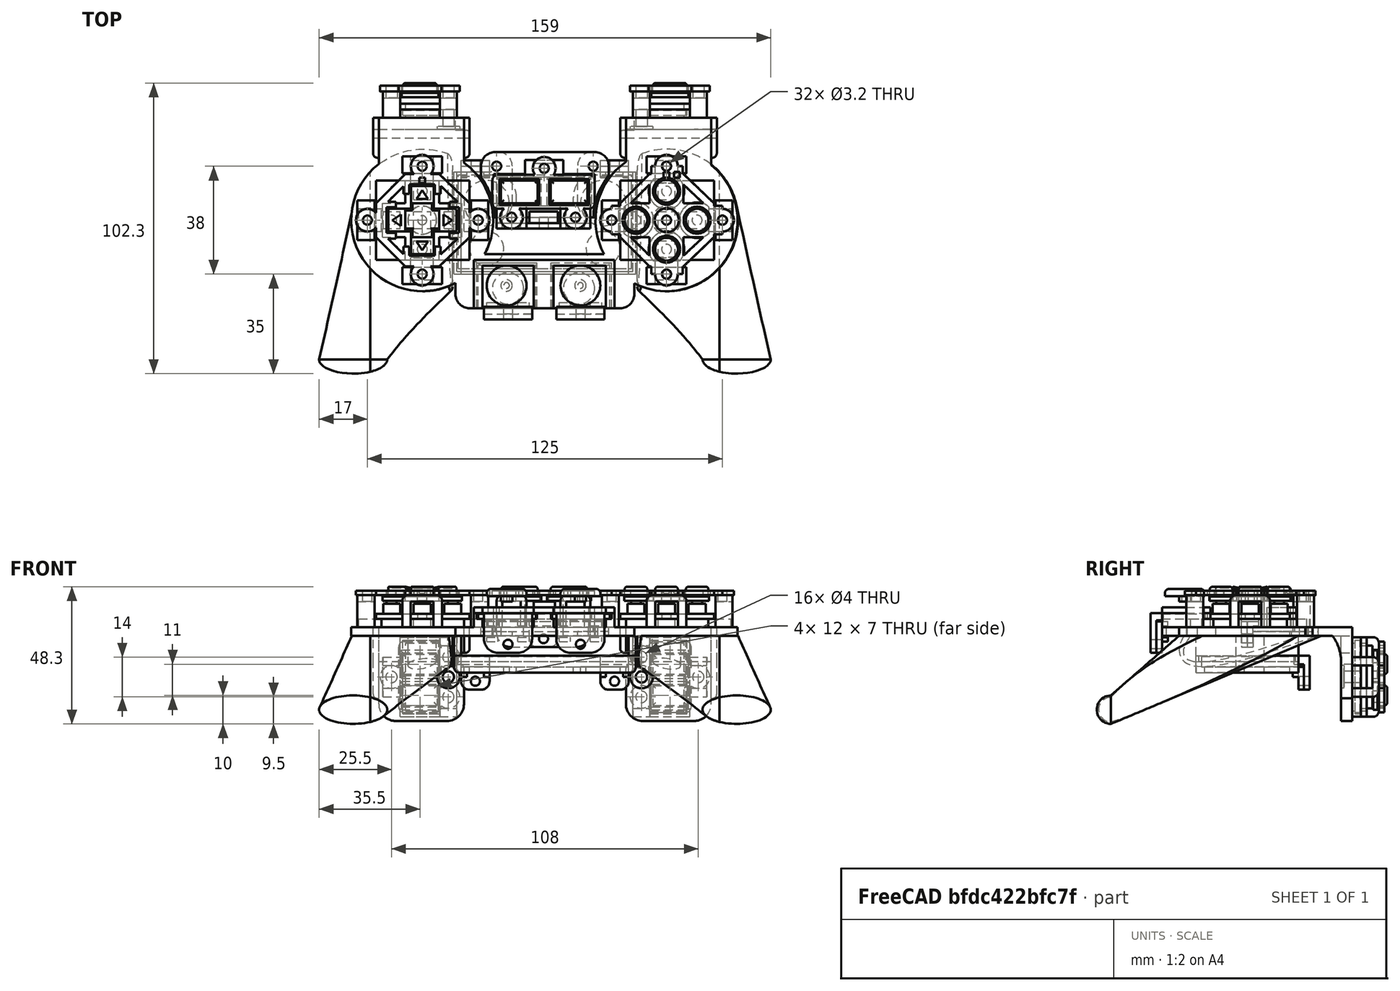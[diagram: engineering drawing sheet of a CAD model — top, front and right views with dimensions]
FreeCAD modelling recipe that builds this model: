
FCSTD DOCUMENT  (FreeCAD 0.18R16131 (Git))
Label: Game_Controller_V4
License: CC-BY 3.0
LicenseURL: http://creativecommons.org/licenses/by/3.0/
objects: Part::Box×211, Part::Cut×117, Part::Cylinder×100, Part::MultiFuse×68, Part::Fillet×61, Part::Feature×41, Part::Loft×16, App::DocumentObjectGroup×13, Part::MultiCommon×2, Part::Circle×1, Part::Ellipsoid×1, Part::Ellipse×1, Part::Sweep×1, Part::Mirroring×1
note: 621 computed .brp shape members not serialized (recipe doc carries the construction recipe); baked Part::Feature solids carry a one-line shape summary decoded from their .brp

FEATURE [Part::Box] Box  label="Btnlft_Base"
  AttacherType = Attacher::AttachEngine3D
  Height = 3.6
  Length = 6
  Width = 6
FEATURE [Part::Cylinder] Cylinder  label="Btnlft_Top"
  Angle = 360
  AttacherType = Attacher::AttachEngine3D
  Height = 1
  Placement = pos=(3,3,3.6) rot=(0,0,1;0rad)
  Radius = 1.75
FEATURE [Part::MultiFuse] Fusion  label="Btnlft"
  Placement = pos=(2.54,11,1.7) rot=(0,0,1;0rad)
  Shapes = -> [Box,Cylinder]
FEATURE [Part::Box] Box001  label="Dpad_Base"
  AttacherType = Attacher::AttachEngine3D
  Height = 1.7
  Length = 33
  Width = 28
FEATURE [Part::Cylinder] Cylinder001  label="Btnrt_Top"
  Angle = 360
  AttacherType = Attacher::AttachEngine3D
  Height = 1
  Placement = pos=(3,3,3.6) rot=(0,0,1;0rad)
  Radius = 1.75
FEATURE [Part::Box] Box002  label="Bntrt_Base"
  AttacherType = Attacher::AttachEngine3D
  Height = 3.6
  Length = 6
  Width = 6
FEATURE [Part::MultiFuse] Fusion001  label="Btnrt"
  Placement = pos=(24.07,11,1.7) rot=(0,0,1;0rad)
  Shapes = -> [Box002,Cylinder001]
FEATURE [Part::Cylinder] Cylinder002  label="Btnup_Top"
  Angle = 360
  AttacherType = Attacher::AttachEngine3D
  Height = 1
  Placement = pos=(3,3,3.6) rot=(0,0,1;0rad)
  Radius = 1.75
FEATURE [Part::Box] Box003  label="Btnup_Base"
  AttacherType = Attacher::AttachEngine3D
  Height = 3.6
  Length = 6
  Width = 6
FEATURE [Part::MultiFuse] Fusion002  label="Btnup"
  Placement = pos=(13.31,21.21,1.7) rot=(0,0,1;0rad)
  Shapes = -> [Box003,Cylinder002]
FEATURE [Part::Cylinder] Cylinder003  label="Btndn_Top"
  Angle = 360
  AttacherType = Attacher::AttachEngine3D
  Height = 1
  Placement = pos=(3,3,3.6) rot=(0,0,1;0rad)
  Radius = 1.75
FEATURE [Part::Box] Box004  label="Btndn_Base"
  AttacherType = Attacher::AttachEngine3D
  Height = 3.6
  Length = 6
  Width = 6
FEATURE [Part::MultiFuse] Fusion003  label="Btndn"
  Placement = pos=(13.31,0.787,1.7) rot=(0,0,1;0rad)
  Shapes = -> [Box004,Cylinder003]
FEATURE [Part::Cylinder] Cylinder004  label="Dpad_Center_Hole"
  Angle = 360
  AttacherType = Attacher::AttachEngine3D
  Height = 2
  Placement = pos=(16.31,14,0) rot=(0,0,1;0rad)
  Radius = 1.588
FEATURE [Part::Cut] Cut  label="Dpad_PCB_1"
  Base = -> Box001
  Tool = -> Cylinder004
FEATURE [Part::MultiFuse] Fusion004  label="Dpad_PCB"
  Shapes = -> [Fusion,Fusion001,Fusion002,Fusion003,Cut]
FEATURE [Part::Box] Box005  label="Dpad5"
  AttacherType = Attacher::AttachEngine3D
  Height = 1.5
  Length = 12
  Placement = pos=(6,-10,0) rot=(0,0,1;0rad)
  Width = 8
FEATURE [Part::Box] Box006  label="Dpad4"
  AttacherType = Attacher::AttachEngine3D
  Height = 1.5
  Length = 12
  Placement = pos=(6,10,0) rot=(0,0,1;0rad)
  Width = 8
FEATURE [Part::Box] Box007  label="Dpad3"
  AttacherType = Attacher::AttachEngine3D
  Height = 1.5
  Length = 10
  Placement = pos=(16,-2,0) rot=(0,0,1;0rad)
  Width = 12
FEATURE [Part::Box] Box008  label="Dpad2"
  AttacherType = Attacher::AttachEngine3D
  Height = 1.5
  Length = 10
  Placement = pos=(-2,-2,0) rot=(0,0,1;0rad)
  Width = 12
FEATURE [Part::Fillet] Fillet  label="Dpad1"
  Edges = 36 edges r=0.5: [Edge1,Edge2,Edge3,Edge5,Edge6,Edge9,Edge11,Edge19,Edge22,Edge25,Edge26,Edge28,Edge29,Edge35,Edge48,Edge49,Edge50,Edge58,Edge59,Edge63,Edge70,Edge71,Edge82,Edge87,Edge88,Edge91,Edge101,Edge103,Edge109,Edge117,Edge118,Edge119,Edge120,Edge121,Edge122,Edge123]
FEATURE [Part::MultiFuse] Fusion006  label="Dpad_Assembly"
  Placement = pos=(4.31,10,6.3) rot=(0,0,1;0rad)
  Shapes = -> [Fillet,Box008,Box007,Box006,Box005]
FEATURE [Part::Cylinder] Cylinder005  label="Cylinder"
  Angle = 360
  AttacherType = Attacher::AttachEngine3D
  Height = 1.5
  Placement = pos=(-3,14,8.3) rot=(0,0,1;0rad)
  Radius = 1.6
FEATURE [Part::Cylinder] Cylinder006  label="Cylinder001"
  Angle = 360
  AttacherType = Attacher::AttachEngine3D
  Height = 1.5
  Placement = pos=(-3,14,8.3) rot=(0,0,1;0rad)
  Radius = 4
FEATURE [Part::Box] Box013  label="Cube004"
  AttacherType = Attacher::AttachEngine3D
  Height = 1.5
  Length = 4
  Placement = pos=(3,7.5,8.3) rot=(0,0,1;0rad)
  Width = 2
FEATURE [Part::Box] Box014  label="Cube005"
  AttacherType = Attacher::AttachEngine3D
  Height = 1.5
  Length = 4
  Placement = pos=(3,18.5,8.3) rot=(0,0,1;0rad)
  Width = 2
FEATURE [Part::Box] Box015  label="Cube006"
  AttacherType = Attacher::AttachEngine3D
  Height = 1.5
  Length = 4
  Placement = pos=(26,7.5,8.3) rot=(0,0,1;0rad)
  Width = 2
FEATURE [Part::Box] Box016  label="Cube007"
  AttacherType = Attacher::AttachEngine3D
  Height = 1.5
  Length = 4
  Placement = pos=(26,18.5,8.3) rot=(0,0,1;0rad)
  Width = 2
FEATURE [Part::Box] Box017  label="Cube008"
  AttacherType = Attacher::AttachEngine3D
  Height = 1.5
  Length = 4
  Placement = pos=(11.75,0.75,8.3) rot=(0,0,1;1.5708rad)
  Width = 2
FEATURE [Part::Box] Box018  label="Cube009"
  AttacherType = Attacher::AttachEngine3D
  Height = 1.5
  Length = 4
  Placement = pos=(22.75,0.75,8.3) rot=(0,0,1;1.5708rad)
  Width = 2
FEATURE [Part::Box] Box019  label="Cube010"
  AttacherType = Attacher::AttachEngine3D
  Height = 1.5
  Length = 4
  Placement = pos=(11.75,23.2,8.3) rot=(0,0,1;1.5708rad)
  Width = 2
FEATURE [Part::Box] Box020  label="Cube011"
  AttacherType = Attacher::AttachEngine3D
  Height = 1.5
  Length = 4
  Placement = pos=(22.75,23.2,8.3) rot=(0,0,1;1.5708rad)
  Width = 2
FEATURE [Part::Box] Box011  label="Cube002"
  AttacherType = Attacher::AttachEngine3D
  Height = 1.5
  Length = 3.75
  Placement = pos=(29.25,8,8.3) rot=(0,0,1;0rad)
  Width = 12
FEATURE [Part::Box] Box010  label="DpadR3"
  AttacherType = Attacher::AttachEngine3D
  Height = 1.5
  Length = 12
  Placement = pos=(10.31,26.5,8.3) rot=(0,0,1;0rad)
  Width = 3.75
FEATURE [Part::Box] Box012  label="Cube003"
  AttacherType = Attacher::AttachEngine3D
  Height = 1.5
  Length = 12
  Placement = pos=(10.31,-2.25,8.3) rot=(0,0,1;0rad)
  Width = 3.75
FEATURE [Part::Box] Box009  label="Cube"
  AttacherType = Attacher::AttachEngine3D
  Height = 1.5
  Length = 3.75
  Placement = pos=(0,8,8.3) rot=(0,0,1;0rad)
  Width = 12
FEATURE [Part::Feature] Solid
  shape: bbox 10.69 x 10.25 x 1.5 mm, 6 faces (baked)
FEATURE [Part::Feature] Solid002
  shape: bbox 10.69 x 10.25 x 1.5 mm, 6 faces (baked)
FEATURE [Part::Feature] Solid003
  shape: bbox 10.31 x 10.25 x 1.5 mm, 6 faces (baked)
FEATURE [Part::Feature] Solid004
  shape: bbox 10.31 x 10.25 x 1.5 mm, 6 faces (baked)
FEATURE [Part::Cylinder] Cylinder007  label="Cylinder002"
  Angle = 360
  AttacherType = Attacher::AttachEngine3D
  Height = 1.5
  Placement = pos=(16.3,33,8.3) rot=(0,0,1;0rad)
  Radius = 4
FEATURE [Part::Cylinder] Cylinder008  label="Cylinder003"
  Angle = 360
  AttacherType = Attacher::AttachEngine3D
  Height = 1.5
  Placement = pos=(16.3,33,8.3) rot=(0,0,1;0rad)
  Radius = 1.6
FEATURE [Part::Cut] Cut001
  Base = -> Cylinder007
  Tool = -> Cylinder008
FEATURE [Part::Cut] Cut002
  Base = -> Cylinder006
  Tool = -> Cylinder005
FEATURE [Part::Cylinder] Cylinder009  label="Cylinder015"
  Angle = 360
  AttacherType = Attacher::AttachEngine3D
  Height = 1.5
  Placement = pos=(16.3,33,8.3) rot=(0,0,1;0rad)
  Radius = 1.6
FEATURE [Part::Cylinder] Cylinder010  label="Cylinder107"
  Angle = 360
  AttacherType = Attacher::AttachEngine3D
  Height = 1.5
  Placement = pos=(16.3,33,8.3) rot=(0,0,1;0rad)
  Radius = 4
FEATURE [Part::Cut] Cut003
  Base = -> Cylinder010
  Placement = pos=(0,-38,0) rot=(0,0,1;0rad)
  Tool = -> Cylinder009
FEATURE [Part::Cylinder] Cylinder011  label="Cylinder108"
  Angle = 360
  AttacherType = Attacher::AttachEngine3D
  Height = 1.5
  Placement = pos=(-3,14,8.3) rot=(0,0,1;0rad)
  Radius = 1.6
FEATURE [Part::Cylinder] Cylinder012  label="Cylinder109"
  Angle = 360
  AttacherType = Attacher::AttachEngine3D
  Height = 1.5
  Placement = pos=(-3,14,8.3) rot=(0,0,1;0rad)
  Radius = 4
FEATURE [Part::Cut] Cut004
  Base = -> Cylinder012
  Placement = pos=(39,0,0) rot=(0,0,1;0rad)
  Tool = -> Cylinder011
FEATURE [Part::Box] Box021  label="Cube012"
  AttacherType = Attacher::AttachEngine3D
  Height = 1.5
  Length = 2
  Placement = pos=(15.3,27,9) rot=(0,0,1;0rad)
  Width = 2
FEATURE [Part::MultiFuse] Fusion007
  Shapes = -> [Cut004,Cut003,Cut002,Cut001,Solid003,Solid004,Solid002,Box010,Box011,Solid,Box012,Box009,Box020,Box015,Box016,Box018,Box017,Box013,Box014,Box019]
FEATURE [Part::Cut] Cut005  label="Dpad_Retainer_Initial"
  Base = -> Fusion007
  Tool = -> Box021
FEATURE [Part::Box] Box022  label="Main_PCB"
  AttacherType = Attacher::AttachEngine3D
  Height = 1.7
  Length = 60.96
  Placement = pos=(29,-3,-15) rot=(0,0,1;0rad)
  Width = 33.02
FEATURE [Part::Cut] Cut006  label="Main_Buttons_PCB_1"
  Base = -> Box001
  Tool = -> Cylinder004
FEATURE [Part::MultiFuse] Fusion009  label="Btn3"
  Placement = pos=(13.31,0.787,1.7) rot=(0,0,1;0rad)
  Shapes = -> [Box004,Cylinder003]
FEATURE [Part::MultiFuse] Fusion010  label="Btn1"
  Placement = pos=(13.31,21.21,1.7) rot=(0,0,1;0rad)
  Shapes = -> [Box003,Cylinder002]
FEATURE [Part::MultiFuse] Fusion011  label="Btn2"
  Placement = pos=(24.07,11,1.7) rot=(0,0,1;0rad)
  Shapes = -> [Box002,Cylinder001]
FEATURE [Part::MultiFuse] Fusion012  label="Btn4"
  Placement = pos=(2.54,11,1.7) rot=(0,0,1;0rad)
  Shapes = -> [Box,Cylinder]
FEATURE [Part::MultiFuse] Fusion008  label="Main_Buttons_PCB"
  Placement = pos=(86,0,0) rot=(0,0,1;0rad)
  Shapes = -> [Fusion012,Fusion011,Fusion010,Fusion009,Cut006]
FEATURE [Part::Cylinder] Cylinder013  label="Cylinder110"
  Angle = 360
  AttacherType = Attacher::AttachEngine3D
  Height = 5
  Placement = pos=(120.31,24.21,6.3) rot=(0,0,1;0rad)
  Radius = 4
FEATURE [Part::Cylinder] Cylinder014  label="Btn1_Base"
  Angle = 360
  AttacherType = Attacher::AttachEngine3D
  Height = 1.5
  Placement = pos=(120.31,24.21,6.3) rot=(0,0,1;0rad)
  Radius = 6.25
FEATURE [Part::Fillet] Fillet001  label="Btn1_Top"
  Base = -> Cylinder013
  Edges = 1 edges r=1: [Edge1]
FEATURE [Part::Cylinder] Cylinder016  label="Btn4_Base"
  Angle = 360
  AttacherType = Attacher::AttachEngine3D
  Height = 1.5
  Placement = pos=(109.54,14,6.3) rot=(0,0,1;0rad)
  Radius = 6.25
FEATURE [Part::Cylinder] Cylinder017  label="Cylinder111"
  Angle = 360
  AttacherType = Attacher::AttachEngine3D
  Height = 5
  Placement = pos=(109.54,14,6.3) rot=(0,0,1;0rad)
  Radius = 4
FEATURE [Part::Fillet] Fillet002  label="Btn4_Top"
  Base = -> Cylinder017
  Edges = 1 edges r=1: [Edge1]
FEATURE [Part::Cylinder] Cylinder018  label="Btn2_Base"
  Angle = 360
  AttacherType = Attacher::AttachEngine3D
  Height = 1.5
  Placement = pos=(131.07,14,6.3) rot=(0,0,1;0rad)
  Radius = 6.25
FEATURE [Part::Cylinder] Cylinder019  label="Cylinder112"
  Angle = 360
  AttacherType = Attacher::AttachEngine3D
  Height = 5
  Placement = pos=(131.07,14,6.3) rot=(0,0,1;0rad)
  Radius = 4
FEATURE [Part::Fillet] Fillet003  label="Btn2_Top"
  Base = -> Cylinder019
  Edges = 1 edges r=1: [Edge1]
FEATURE [Part::Cylinder] Cylinder020  label="Btn3_Base"
  Angle = 360
  AttacherType = Attacher::AttachEngine3D
  Height = 1.5
  Placement = pos=(120.31,3.79,6.3) rot=(0,0,1;0rad)
  Radius = 6.25
FEATURE [Part::Cylinder] Cylinder021  label="Cylinder113"
  Angle = 360
  AttacherType = Attacher::AttachEngine3D
  Height = 5
  Placement = pos=(120.31,3.79,6.3) rot=(0,0,1;0rad)
  Radius = 4
FEATURE [Part::Fillet] Fillet004  label="Btn3_Top"
  Base = -> Cylinder021
  Edges = 1 edges r=1: [Edge1]
FEATURE [Part::MultiFuse] Fusion013  label="Btn1_Assembly"
  Placement = pos=(-18,0,0) rot=(0,0,1;0rad)
  Shapes = -> [Cylinder014,Fillet001]
FEATURE [Part::MultiFuse] Fusion014  label="Btn2_Assembly"
  Placement = pos=(-18,0,0) rot=(0,0,1;0rad)
  Shapes = -> [Cylinder018,Fillet003]
FEATURE [Part::MultiFuse] Fusion015  label="Btn3_Assembly"
  Placement = pos=(-18,0,0) rot=(0,0,1;0rad)
  Shapes = -> [Cylinder020,Fillet004]
FEATURE [Part::MultiFuse] Fusion016  label="Btn4_Assembly"
  Placement = pos=(-18,0,0) rot=(0,0,1;0rad)
  Shapes = -> [Cylinder016,Fillet002]
FEATURE [Part::Cylinder] Cylinder022  label="Cylinder114"
  Angle = 360
  AttacherType = Attacher::AttachEngine3D
  Height = 1.5
  Placement = pos=(-3,14,8.3) rot=(0,0,1;0rad)
  Radius = 4
FEATURE [Part::Cylinder] Cylinder023  label="Cylinder115"
  Angle = 360
  AttacherType = Attacher::AttachEngine3D
  Height = 1.5
  Placement = pos=(-3,14,8.3) rot=(0,0,1;0rad)
  Radius = 1.6
FEATURE [Part::Cylinder] Cylinder024  label="Cylinder116"
  Angle = 360
  AttacherType = Attacher::AttachEngine3D
  Height = 1.5
  Placement = pos=(16.3,33,8.3) rot=(0,0,1;0rad)
  Radius = 4
FEATURE [Part::Cylinder] Cylinder025  label="Cylinder117"
  Angle = 360
  AttacherType = Attacher::AttachEngine3D
  Height = 1.5
  Placement = pos=(16.3,33,8.3) rot=(0,0,1;0rad)
  Radius = 1.6
FEATURE [Part::Cut] Cut009
  Base = -> Cylinder024
  Placement = pos=(104,-38,0) rot=(0,0,1;0rad)
  Tool = -> Cylinder025
FEATURE [Part::Cylinder] Cylinder026  label="Cylinder118"
  Angle = 360
  AttacherType = Attacher::AttachEngine3D
  Height = 1.5
  Placement = pos=(-3,14,8.3) rot=(0,0,1;0rad)
  Radius = 4
FEATURE [Part::Cylinder] Cylinder027  label="Cylinder119"
  Angle = 360
  AttacherType = Attacher::AttachEngine3D
  Height = 1.5
  Placement = pos=(-3,14,8.3) rot=(0,0,1;0rad)
  Radius = 1.6
FEATURE [Part::Cut] Cut010
  Base = -> Cylinder026
  Placement = pos=(104,0,0) rot=(0,0,1;0rad)
  Tool = -> Cylinder027
FEATURE [Part::Cylinder] Cylinder028  label="Cylinder120"
  Angle = 360
  AttacherType = Attacher::AttachEngine3D
  Height = 1.5
  Placement = pos=(16.3,33,8.3) rot=(0,0,1;0rad)
  Radius = 4
FEATURE [Part::Cylinder] Cylinder029  label="Cylinder121"
  Angle = 360
  AttacherType = Attacher::AttachEngine3D
  Height = 1.5
  Placement = pos=(16.3,33,8.3) rot=(0,0,1;0rad)
  Radius = 1.6
FEATURE [Part::Cut] Cut011
  Base = -> Cylinder028
  Placement = pos=(104,0,0) rot=(0,0,1;0rad)
  Tool = -> Cylinder029
FEATURE [Part::Feature] Solid005
  Placement = pos=(104,0,0) rot=(0,0,1;0rad)
  shape: bbox 10.31 x 10.25 x 1.5 mm, 6 faces (baked)
FEATURE [Part::Feature] Solid006
  Placement = pos=(104,0,0) rot=(0,0,1;0rad)
  shape: bbox 10.31 x 10.25 x 1.5 mm, 6 faces (baked)
FEATURE [Part::Feature] Solid007
  Placement = pos=(104,0,0) rot=(0,0,1;0rad)
  shape: bbox 10.69 x 10.25 x 1.5 mm, 6 faces (baked)
FEATURE [Part::Box] Box023  label="DpadR004"
  AttacherType = Attacher::AttachEngine3D
  Height = 1.5
  Length = 12
  Placement = pos=(114.31,13.5,8.3) rot=(0,0,1;0rad)
  Width = 16.75
FEATURE [Part::Box] Box024  label="Cube014"
  AttacherType = Attacher::AttachEngine3D
  Height = 1.5
  Length = 11.75
  Placement = pos=(125.25,8,8.3) rot=(0,0,1;0rad)
  Width = 12
FEATURE [Part::Feature] Solid008
  Placement = pos=(104,0,0) rot=(0,0,1;0rad)
  shape: bbox 10.69 x 10.25 x 1.5 mm, 6 faces (baked)
FEATURE [Part::Box] Box025  label="Cube015"
  AttacherType = Attacher::AttachEngine3D
  Height = 1.5
  Length = 12
  Placement = pos=(114.31,-2.25,8.3) rot=(0,0,1;0rad)
  Width = 16.75
FEATURE [Part::Box] Box026  label="Cube016"
  AttacherType = Attacher::AttachEngine3D
  Height = 1.5
  Length = 11
  Placement = pos=(104,8,8.3) rot=(0,0,1;0rad)
  Width = 12
FEATURE [Part::Box] Box035  label="Cube025"
  AttacherType = Attacher::AttachEngine3D
  Height = 1.5
  Length = 2
  Placement = pos=(119.3,29,9) rot=(0,0,1;0rad)
  Width = 2
FEATURE [Part::Cut] Cut008
  Base = -> Cylinder022
  Placement = pos=(143,0,0) rot=(0,0,1;0rad)
  Tool = -> Cylinder023
FEATURE [Part::Cylinder] Cylinder030  label="Btn1_Base001"
  Angle = 360
  AttacherType = Attacher::AttachEngine3D
  Height = 1.5
  Placement = pos=(120.31,24.21,8.3) rot=(0,0,1;0rad)
  Radius = 4.75
FEATURE [Part::MultiFuse] Fusion017
  Shapes = -> [Cut009,Cut010,Cut011,Solid005,Solid006,Solid007,Box023,Box024,Solid008,Box025,Box026]
FEATURE [Part::Cut] Cut012
  Base = -> Fusion017
  Tool = -> Box035
FEATURE [Part::Cut] Cut013
  Base = -> Cut012
  Tool = -> Cylinder030
FEATURE [Part::Cylinder] Cylinder031  label="Btn2_Base001"
  Angle = 360
  AttacherType = Attacher::AttachEngine3D
  Height = 1.5
  Placement = pos=(131.07,14,8.3) rot=(0,0,1;0rad)
  Radius = 4.75
FEATURE [Part::MultiFuse] Fusion018
  Shapes = -> [Cut013,Cut008]
FEATURE [Part::Cut] Cut014
  Base = -> Fusion018
  Tool = -> Cylinder031
FEATURE [Part::Cylinder] Cylinder032  label="Btn3_Base001"
  Angle = 360
  AttacherType = Attacher::AttachEngine3D
  Height = 1.5
  Placement = pos=(120.31,3.79,8.3) rot=(0,0,1;0rad)
  Radius = 4.75
FEATURE [Part::Cut] Cut015
  Base = -> Cut014
  Tool = -> Cylinder032
FEATURE [Part::Cylinder] Cylinder033  label="Btn4_Base001"
  Angle = 360
  AttacherType = Attacher::AttachEngine3D
  Height = 1.5
  Placement = pos=(109.54,14,8.3) rot=(0,0,1;0rad)
  Radius = 4.75
FEATURE [Part::Cut] Cut016
  Base = -> Cut015
  Tool = -> Cylinder033
FEATURE [Part::Cylinder] Cylinder034  label="Btn4_Base002"
  Angle = 360
  AttacherType = Attacher::AttachEngine3D
  Height = 1.5
  Placement = pos=(120.4,14,8.3) rot=(0,0,1;0rad)
  Radius = 4.25
FEATURE [Part::Cut] Cut017  label="Main_Buttons_Retainer1"
  Base = -> Cut016
  Tool = -> Cylinder034
FEATURE [Part::Box] Box036  label="Cube026"
  AttacherType = Attacher::AttachEngine3D
  Height = 1.5
  Length = 3
  Placement = pos=(101,9,8.3) rot=(0,0,1;0rad)
  Width = 3
FEATURE [Part::Box] Box037  label="Cube027"
  AttacherType = Attacher::AttachEngine3D
  Height = 1.5
  Length = 3
  Placement = pos=(101,16,8.3) rot=(0,0,1;0rad)
  Width = 3
FEATURE [Part::Box] Box038  label="Cube028"
  AttacherType = Attacher::AttachEngine3D
  Height = 1.5
  Length = 3
  Placement = pos=(137,9,8.3) rot=(0,0,1;0rad)
  Width = 3
FEATURE [Part::Box] Box039  label="Cube029"
  AttacherType = Attacher::AttachEngine3D
  Height = 1.5
  Length = 3
  Placement = pos=(137,16,8.3) rot=(0,0,1;0rad)
  Width = 3
FEATURE [Part::Box] Box040  label="Cube030"
  AttacherType = Attacher::AttachEngine3D
  Height = 1.5
  Length = 3
  Placement = pos=(115,-5,8.3) rot=(0,0,1;0rad)
  Width = 3
FEATURE [Part::Box] Box041  label="Cube031"
  AttacherType = Attacher::AttachEngine3D
  Height = 1.5
  Length = 3
  Placement = pos=(123,-5,8.3) rot=(0,0,1;0rad)
  Width = 3
FEATURE [Part::Box] Box042  label="Cube032"
  AttacherType = Attacher::AttachEngine3D
  Height = 1.5
  Length = 3
  Placement = pos=(115,30,8.3) rot=(0,0,1;0rad)
  Width = 3
FEATURE [Part::Box] Box043  label="Cube033"
  AttacherType = Attacher::AttachEngine3D
  Height = 1.5
  Length = 3
  Placement = pos=(123,30,8.3) rot=(0,0,1;0rad)
  Width = 3
FEATURE [Part::MultiFuse] Fusion019  label="Main_Buttons_Retainer_Initial"
  Placement = pos=(-18,0,0) rot=(0,0,1;0rad)
  Shapes = -> [Cut017,Box036,Box037,Box038,Box039,Box040,Box041,Box042,Box043]
FEATURE [Part::Cylinder] Cylinder035  label="Cylinder122"
  Angle = 360
  AttacherType = Attacher::AttachEngine3D
  Height = 3
  Placement = pos=(16.3,14,-6) rot=(0,0,1;0rad)
  Radius = 25
FEATURE [Part::Box] Box044  label="Cube034"
  AttacherType = Attacher::AttachEngine3D
  Height = 3
  Length = 8
  Placement = pos=(12.3,-7,-3) rot=(0,0,1;0rad)
  Width = 8
FEATURE [Part::Box] Box045  label="Cube035"
  AttacherType = Attacher::AttachEngine3D
  Height = 3
  Length = 8
  Placement = pos=(12.3,27,-3) rot=(0,0,1;0rad)
  Width = 8
FEATURE [Part::Box] Box046  label="Cube036"
  AttacherType = Attacher::AttachEngine3D
  Height = 3
  Length = 8
  Placement = pos=(-6,10,-3) rot=(0,0,1;0rad)
  Width = 8
FEATURE [Part::Box] Box047  label="Cube037"
  AttacherType = Attacher::AttachEngine3D
  Height = 3
  Length = 8
  Placement = pos=(31,10,-3) rot=(0,0,1;0rad)
  Width = 8
FEATURE [Part::Box] Box048  label="Cube038"
  AttacherType = Attacher::AttachEngine3D
  Height = 3
  Length = 6
  Placement = pos=(13.3,11,-3) rot=(0,0,1;0rad)
  Width = 6
FEATURE [Part::Cylinder] Cylinder036  label="Cylinder123"
  Angle = 360
  AttacherType = Attacher::AttachEngine3D
  Height = 3
  Placement = pos=(124.3,14,-6) rot=(0,0,1;0rad)
  Radius = 25
FEATURE [Part::Box] Box049  label="Cube039"
  AttacherType = Attacher::AttachEngine3D
  Height = 3
  Length = 8
  Placement = pos=(120.3,27,-3) rot=(0,0,1;0rad)
  Width = 8
FEATURE [Part::Box] Box050  label="Cube040"
  AttacherType = Attacher::AttachEngine3D
  Height = 3
  Length = 8
  Placement = pos=(120.3,-7,-3) rot=(0,0,1;0rad)
  Width = 8
FEATURE [Part::Box] Box051  label="Cube041"
  AttacherType = Attacher::AttachEngine3D
  Height = 3
  Length = 8
  Placement = pos=(102,10,-3) rot=(0,0,1;0rad)
  Width = 8
FEATURE [Part::Box] Box052  label="Cube042"
  AttacherType = Attacher::AttachEngine3D
  Height = 3
  Length = 8
  Placement = pos=(139,10,-3) rot=(0,0,1;0rad)
  Width = 8
FEATURE [Part::Box] Box053  label="Cube043"
  AttacherType = Attacher::AttachEngine3D
  Height = 3
  Length = 6
  Placement = pos=(121.3,11,-3) rot=(0,0,1;0rad)
  Width = 6
FEATURE [Part::Box] Box054  label="Middle_Buttons"
  AttacherType = Attacher::AttachEngine3D
  Height = 1.7
  Length = 33.02
  Placement = pos=(42.7,19,0) rot=(0,0,1;0rad)
  Width = 10.16
FEATURE [Part::Box] Box055  label="Left_Analog_PCB"
  AttacherType = Attacher::AttachEngine3D
  Height = 1.7
  Length = 20.32
  Placement = pos=(36,-17,0) rot=(0,0,1;0rad)
  Width = 15.24
FEATURE [Part::Box] Box056  label="Right_Analog_PCB"
  AttacherType = Attacher::AttachEngine3D
  Height = 1.7
  Length = 20.32
  Placement = pos=(62,-17,0) rot=(0,0,1;0rad)
  Width = 15.24
FEATURE [Part::Box] Box063  label="Cube053"
  AttacherType = Attacher::AttachEngine3D
  Height = 3
  Length = 30
  Placement = pos=(1,33,-6) rot=(0,0,1;0rad)
  Width = 17
FEATURE [Part::Box] Box064  label="Cube054"
  AttacherType = Attacher::AttachEngine3D
  Height = 3
  Length = 30
  Placement = pos=(110,33,-6) rot=(0,0,1;0rad)
  Width = 17
FEATURE [Part::Circle] Circle
  Angle0 = 0
  Angle1 = 360
  AttacherType = Attacher::AttachEngine3D
  Placement = pos=(16.5,14,-8) rot=(0,0,1;0rad)
  Radius = 25
FEATURE [Part::Feature] Edge
  shape: bbox 37.5 x 49 x 26 mm, 0 faces, 0 solids (baked)
FEATURE [Part::Ellipsoid] Ellipsoid001
  Angle1 = -90
  Angle2 = 90
  Angle3 = 180
  AttacherType = Attacher::AttachEngine3D
  Placement = pos=(149,-35,-32) rot=(0.707107,0,-0.707107;3.14159rad)
  Radius1 = 12
  Radius2 = 5
  Radius3 = 0
FEATURE [Part::Ellipse] Ellipse
  Angle0 = 0
  Angle1 = 360
  AttacherType = Attacher::AttachEngine3D
  MajorRadius = 12
  MinorRadius = 5
  Placement = pos=(-8,-35,18) rot=(-1,0,0;1.5708rad)
FEATURE [Part::Sweep] Sweep
  Frenet = false
  Placement = pos=(141,0,-14) rot=(0,1,0;3.14159rad)
  Sections = -> [Circle,Ellipse]
  Solid = true
  Spine = -> Edge [Edge1]
  Transition = 1
FEATURE [Part::MultiFuse] Fusion020
  Shapes = -> [Ellipsoid001,Sweep,Circle,Ellipse]
FEATURE [Part::Mirroring] Part__Mirroring  label="Fusion020 (Mirror #1)"
  Base = (0,0,0)
  Normal = (1,0,0)
  Placement = pos=(141,0,0) rot=(0,0,1;0rad)
  Source = -> Fusion020
FEATURE [Part::Box] Box065  label="Cube055"
  AttacherType = Attacher::AttachEngine3D
  Height = 50
  Length = 50
  Placement = pos=(-2,-44,-41) rot=(0,0,1;0rad)
  Width = 100
FEATURE [Part::Cut] Cut018  label="Left_Handle_Left_Side"
  Base = -> Part__Mirroring
  Tool = -> Box065
FEATURE [Part::MultiCommon] Common  label="Left_Handle_Right_Side_1"
  Shapes = -> [Box065,Part__Mirroring]
FEATURE [Part::Cylinder] Cylinder037  label="Cylinder124"
  Angle = 360
  AttacherType = Attacher::AttachEngine3D
  Height = 10
  Placement = pos=(16.31,14,-8) rot=(0,0,1;0rad)
  Radius = 1.6
FEATURE [Part::Cylinder] Cylinder038  label="Cylinder125"
  Angle = 360
  AttacherType = Attacher::AttachEngine3D
  Height = 20
  Placement = pos=(124.31,14,-20) rot=(0,0,1;0rad)
  Radius = 5
FEATURE [Part::Cut] Cut020  label="Left_Handle_Right_Side_01"
  Base = -> Common
  Tool = -> Cylinder038
FEATURE [Part::Box] Box066  label="Cube056"
  AttacherType = Attacher::AttachEngine3D
  Height = 50
  Length = 50
  Placement = pos=(143,-44,-41) rot=(0,0,1;0rad)
  Width = 100
FEATURE [Part::Cut] Cut021  label="Right_Handle_Left_Side_1"
  Base = -> Fusion020
  Tool = -> Box066
FEATURE [Part::Cut] Cut022  label="Right_Handle_Left_Side_001"
  Base = -> Cut021
  Placement = pos=(-22,0,0) rot=(0,0,1;0rad)
  Tool = -> Cylinder038
FEATURE [Part::MultiCommon] Common001  label="Right_Handle_Right_Side"
  Placement = pos=(-22,0,0) rot=(0,0,1;0rad)
  Shapes = -> [Fusion020,Box066]
FEATURE [Part::Cylinder] Cylinder039  label="Cylinder126"
  Angle = 360
  AttacherType = Attacher::AttachEngine3D
  Height = 20
  Placement = pos=(16.31,14,-20) rot=(0,0,1;0rad)
  Radius = 5
FEATURE [Part::Cut] Cut023  label="Left_Handle_Right_Side_001"
  Base = -> Cut020
  Tool = -> Cylinder039
FEATURE [Part::Cylinder] Cylinder040  label="Cylinder127"
  Angle = 360
  AttacherType = Attacher::AttachEngine3D
  Height = 10
  Placement = pos=(124.31,14,-8) rot=(0,0,1;0rad)
  Radius = 1.6
FEATURE [Part::Box] Box072  label="Cube062"
  AttacherType = Attacher::AttachEngine3D
  Height = 9
  Length = 30
  Placement = pos=(1,40,-15) rot=(0,0,1;0rad)
  Width = 6
FEATURE [Part::Cylinder] Cylinder041  label="Cylinder128"
  Angle = 360
  AttacherType = Attacher::AttachEngine3D
  Height = 32
  Placement = pos=(0,31,-15) rot=(0,1,0;1.5708rad)
  Radius = 15
FEATURE [Part::Box] Box073  label="Cube063"
  AttacherType = Attacher::AttachEngine3D
  Height = 30
  Length = 30
  Placement = pos=(1,46,-36) rot=(0,0,1;0rad)
  Width = 4
FEATURE [Part::Box] Box078  label="Cube068"
  AttacherType = Attacher::AttachEngine3D
  Height = 2.3
  Length = 14
  Placement = pos=(9.3,-8.5,6) rot=(0,0,1;0rad)
  Width = 6
FEATURE [Part::Cylinder] Cylinder042  label="Cylinder097"
  Angle = 360
  AttacherType = Attacher::AttachEngine3D
  Height = 3
  Placement = pos=(16.3,-5,6) rot=(0,0,1;0rad)
  Radius = 1.6
FEATURE [Part::Cylinder] Cylinder045  label="Cylinder129"
  Angle = 360
  AttacherType = Attacher::AttachEngine3D
  Height = 4
  Placement = pos=(0,35,-15) rot=(0,1,0;1.5708rad)
  Radius = 15
FEATURE [Part::Box] Box089  label="Cube079"
  AttacherType = Attacher::AttachEngine3D
  Height = 9
  Length = 2
  Placement = pos=(1,44,-15) rot=(0,0,1;0rad)
  Width = 10
FEATURE [Part::Cut] Cut036
  Base = -> Box089
  Placement = pos=(-2,-4,0) rot=(0,0,1;0rad)
  Tool = -> Cylinder045
FEATURE [Part::Box] Box090  label="Cube080"
  AttacherType = Attacher::AttachEngine3D
  Height = 13
  Length = 2
  Placement = pos=(-1,46,-28) rot=(0,0,1;0rad)
  Width = 4
FEATURE [Part::Box] Box091  label="Cube081"
  AttacherType = Attacher::AttachEngine3D
  Height = 3
  Length = 2
  Placement = pos=(-1,36,-6) rot=(0,0,1;0rad)
  Width = 14
FEATURE [Part::MultiFuse] Fusion031
  Shapes = -> [Cut036,Box090,Box091]
FEATURE [Part::Fillet] Fillet011  label="Backplane_Reinforcement_1"
  Base = -> Fusion031
  Edges = 2 edges r=1.5: [Edge2,Edge18]
FEATURE [Part::Box] Box092  label="Cube082"
  AttacherType = Attacher::AttachEngine3D
  Height = 3
  Length = 2
  Placement = pos=(31,36,-6) rot=(0,0,1;0rad)
  Width = 14
FEATURE [Part::Cylinder] Cylinder046  label="Cylinder130"
  Angle = 360
  AttacherType = Attacher::AttachEngine3D
  Height = 4
  Placement = pos=(30,31,-15) rot=(0,1,0;1.5708rad)
  Radius = 15
FEATURE [Part::Box] Box094  label="Cube084"
  AttacherType = Attacher::AttachEngine3D
  Height = 6
  Length = 2
  Placement = pos=(31,40,-12) rot=(0,0,1;0rad)
  Width = 10
FEATURE [Part::Fillet] Fillet012
  Base = -> Box092
  Edges = 1 edges r=1.5: [Edge5]
FEATURE [Part::MultiFuse] Fusion036
  Shapes = -> [Box048,Box047,Box044,Box045,Box063,Box046,Cylinder035]
FEATURE [Part::Cut] Cut040
  Base = -> Fusion036
  Tool = -> Cylinder037
FEATURE [Part::MultiFuse] Fusion037
  Shapes = -> [Box050,Cylinder036,Box051,Box053,Box049,Box052,Box064]
FEATURE [Part::Cut] Cut041
  Base = -> Fusion037
  Placement = pos=(-22,0,0) rot=(0,0,1;0rad)
  Tool = -> Cylinder040
FEATURE [Part::Box] Box076  label="Cube066"
  AttacherType = Attacher::AttachEngine3D
  Height = 9
  Length = 3
  Placement = pos=(9.3,-8.5,-3) rot=(0,0,1;0rad)
  Width = 6
FEATURE [Part::Box] Box077  label="Cube067"
  AttacherType = Attacher::AttachEngine3D
  Height = 9
  Length = 3
  Placement = pos=(20.3,-8.5,-3) rot=(0,0,1;0rad)
  Width = 6
FEATURE [Part::Box] Box105  label="Cube095"
  AttacherType = Attacher::AttachEngine3D
  Height = 9
  Length = 3
  Placement = pos=(9.3,30.5,-3) rot=(0,0,1;0rad)
  Width = 6
FEATURE [Part::Box] Box106  label="Cube096"
  AttacherType = Attacher::AttachEngine3D
  Height = 9
  Length = 3
  Placement = pos=(20.3,30.5,-3) rot=(0,0,1;0rad)
  Width = 6
FEATURE [Part::Box] Box107  label="Cube097"
  AttacherType = Attacher::AttachEngine3D
  Height = 2.3
  Length = 14
  Placement = pos=(9.3,30.5,6) rot=(0,0,1;0rad)
  Width = 6
FEATURE [Part::Cylinder] Cylinder049  label="Cylinder100"
  Angle = 360
  AttacherType = Attacher::AttachEngine3D
  Height = 3
  Placement = pos=(16.3,33,6) rot=(0,0,1;0rad)
  Radius = 1.6
FEATURE [Part::MultiFuse] Fusion039
  Shapes = -> [Box105,Box106,Box107]
FEATURE [Part::Cut] Cut043
  Base = -> Fusion039
  Tool = -> Cylinder049
FEATURE [Part::Box] Box108  label="Cube098"
  AttacherType = Attacher::AttachEngine3D
  Height = 9
  Length = 6
  Placement = pos=(-6.5,18,-3) rot=(0,0,1;0rad)
  Width = 3
FEATURE [Part::Box] Box109  label="Cube099"
  AttacherType = Attacher::AttachEngine3D
  Height = 9
  Length = 6
  Placement = pos=(-6.5,7,-3) rot=(0,0,1;0rad)
  Width = 3
FEATURE [Part::Box] Box110  label="Cube100"
  AttacherType = Attacher::AttachEngine3D
  Height = 2.3
  Length = 6
  Placement = pos=(-6.5,7,6) rot=(0,0,1;0rad)
  Width = 14
FEATURE [Part::Cylinder] Cylinder050  label="Cylinder131"
  Angle = 360
  AttacherType = Attacher::AttachEngine3D
  Height = 3
  Placement = pos=(-3,14,6) rot=(0,0,1;0rad)
  Radius = 1.6
FEATURE [Part::MultiFuse] Fusion040
  Shapes = -> [Box108,Box109,Box110]
FEATURE [Part::Cut] Cut044
  Base = -> Fusion040
  Tool = -> Cylinder050
FEATURE [Part::MultiFuse] Fusion041
  Shapes = -> [Box078,Box077,Box076]
FEATURE [Part::Cut] Cut045
  Base = -> Fusion041
  Tool = -> Cylinder042
FEATURE [Part::Box] Box111  label="Cube101"
  AttacherType = Attacher::AttachEngine3D
  Height = 9
  Length = 6
  Placement = pos=(33.5,18,-3) rot=(0,0,1;0rad)
  Width = 3
FEATURE [Part::Box] Box112  label="Cube102"
  AttacherType = Attacher::AttachEngine3D
  Height = 9
  Length = 6
  Placement = pos=(33.5,7,-3) rot=(0,0,1;0rad)
  Width = 3
FEATURE [Part::Box] Box113  label="Cube103"
  AttacherType = Attacher::AttachEngine3D
  Height = 2.3
  Length = 6
  Placement = pos=(33.5,7,6) rot=(0,0,1;0rad)
  Width = 14
FEATURE [Part::Cylinder] Cylinder051  label="Cylinder132"
  Angle = 360
  AttacherType = Attacher::AttachEngine3D
  Height = 3
  Placement = pos=(36,14,6) rot=(0,0,1;0rad)
  Radius = 1.6
FEATURE [Part::MultiFuse] Fusion042
  Shapes = -> [Box111,Box112,Box113]
FEATURE [Part::Cut] Cut046
  Base = -> Fusion042
  Tool = -> Cylinder051
FEATURE [Part::Fillet] Fillet016
  Base = -> Cut044
  Edges = 2 edges r=2: [Edge19,Edge27]
FEATURE [Part::Fillet] Fillet017
  Base = -> Cut045
  Edges = 2 edges r=2: [Edge3,Edge16]
FEATURE [Part::Fillet] Fillet018
  Base = -> Cut046
  Edges = 2 edges r=2: [Edge19,Edge27]
FEATURE [Part::Fillet] Fillet019
  Base = -> Cut043
  Edges = 2 edges r=2: [Edge14,Edge28]
FEATURE [Part::MultiFuse] Fusion043
  Shapes = -> [Cut040,Fillet016,Fillet017,Fillet018,Fillet019]
FEATURE [Part::Feature] Face
  shape: bbox 47 x 46 x 2e-07 mm, 1 faces, 0 solids (baked)
FEATURE [Part::Feature] Face001
  shape: bbox 51.7 x 50.6 x 2e-07 mm, 1 faces, 0 solids (baked)
FEATURE [Part::Loft] Loft
  Closed = false
  MaxDegree = 5
  Ruled = false
  Sections = -> [Face,Face001]
  Solid = true
FEATURE [Part::Cut] Cut047
  Base = -> Loft
  Tool = -> Cylinder011
FEATURE [Part::Cut] Cut048
  Base = -> Cut047
  Tool = -> Cylinder009
FEATURE [Part::Cylinder] Cylinder052  label="Cylinder133"
  Angle = 360
  AttacherType = Attacher::AttachEngine3D
  Height = 1.5
  Placement = pos=(16.3,-5,8.3) rot=(0,0,1;0rad)
  Radius = 1.6
FEATURE [Part::Cylinder] Cylinder053  label="Cylinder134"
  Angle = 360
  AttacherType = Attacher::AttachEngine3D
  Height = 1.5
  Placement = pos=(36,14,8.3) rot=(0,0,1;0rad)
  Radius = 1.6
FEATURE [Part::Cut] Cut049
  Base = -> Cut048
  Tool = -> Cylinder052
FEATURE [Part::Cut] Cut050
  Base = -> Cut049
  Tool = -> Cylinder053
FEATURE [Part::Feature] Face002
  shape: bbox 28.06 x 27.51 x 2e-07 mm, 1 faces, 0 solids (baked)
FEATURE [Part::Feature] Face003
  shape: bbox 41.67 x 41.63 x 2e-07 mm, 1 faces, 0 solids (baked)
FEATURE [Part::Loft] Loft001
  Closed = false
  MaxDegree = 5
  Ruled = false
  Sections = -> [Face002,Face003]
  Solid = true
FEATURE [Part::Cut] Cut051
  Base = -> Cut050
  Tool = -> Loft001
FEATURE [Part::Cut] Cut052  label="Dpad_Retainer_Final"
  Base = -> Cut051
  Tool = -> Box021
FEATURE [App::DocumentObjectGroup] Group007  label="Dpad_Retainer"
  Group = -> [Cut052,Cut005]
FEATURE [Part::Feature] Face004
  shape: bbox 51.69 x 50.59 x 2e-07 mm, 1 faces, 0 solids (baked)
FEATURE [Part::Feature] Face005
  shape: bbox 51.69 x 50.59 x 2e-07 mm, 1 faces, 0 solids (baked)
FEATURE [Part::Loft] Loft002
  Closed = false
  MaxDegree = 5
  Ruled = false
  Sections = -> [Face004,Face005]
  Solid = true
FEATURE [Part::Feature] Face006
  shape: bbox 15.5 x 12.99 x 2e-07 mm, 1 faces, 0 solids (baked)
FEATURE [Part::Feature] Face007
  shape: bbox 15.5 x 12.99 x 2e-07 mm, 1 faces, 0 solids (baked)
FEATURE [Part::Feature] Face008
  shape: bbox 3.865 x 3.703 x 2e-07 mm, 1 faces, 0 solids (baked)
FEATURE [Part::Feature] Face009
  shape: bbox 3.865 x 3.703 x 2e-07 mm, 1 faces, 0 solids (baked)
FEATURE [Part::Feature] Face010
  shape: bbox 3.756 x 3.556 x 2e-07 mm, 1 faces, 0 solids (baked)
FEATURE [Part::Feature] Face011
  shape: bbox 3.756 x 3.556 x 2e-07 mm, 1 faces, 0 solids (baked)
FEATURE [Part::Feature] Face012
  shape: bbox 11.01 x 10.41 x 2e-07 mm, 1 faces, 0 solids (baked)
FEATURE [Part::Feature] Face013
  shape: bbox 11.01 x 10.41 x 2e-07 mm, 1 faces, 0 solids (baked)
FEATURE [Part::Feature] Face014
  shape: bbox 11.59 x 9.35 x 2e-07 mm, 1 faces, 0 solids (baked)
FEATURE [Part::Feature] Face015
  shape: bbox 11.59 x 9.35 x 2e-07 mm, 1 faces, 0 solids (baked)
FEATURE [Part::Feature] Face016
  shape: bbox 15.45 x 12.67 x 2e-07 mm, 1 faces, 0 solids (baked)
FEATURE [Part::Feature] Face017
  shape: bbox 15.45 x 12.67 x 2e-07 mm, 1 faces, 0 solids (baked)
FEATURE [Part::Feature] Face018
  shape: bbox 15.48 x 13.19 x 2e-07 mm, 1 faces, 0 solids (baked)
FEATURE [Part::Feature] Face019
  shape: bbox 15.48 x 13.19 x 2e-07 mm, 1 faces, 0 solids (baked)
FEATURE [Part::Feature] Face020
  shape: bbox 3.778 x 3.584 x 2e-07 mm, 1 faces, 0 solids (baked)
FEATURE [Part::Feature] Face021
  shape: bbox 3.778 x 3.584 x 2e-07 mm, 1 faces, 0 solids (baked)
FEATURE [Part::Feature] Face022
  shape: bbox 3.706 x 3.489 x 2e-07 mm, 1 faces, 0 solids (baked)
FEATURE [Part::Feature] Face023
  shape: bbox 3.706 x 3.489 x 2e-07 mm, 1 faces, 0 solids (baked)
FEATURE [Part::Loft] Loft003
  Closed = false
  MaxDegree = 5
  Ruled = false
  Sections = -> [Face023,Face022]
  Solid = true
FEATURE [Part::Loft] Loft004
  Closed = false
  MaxDegree = 5
  Ruled = false
  Sections = -> [Face006,Face007]
  Solid = true
FEATURE [Part::Loft] Loft005
  Closed = false
  MaxDegree = 5
  Ruled = false
  Sections = -> [Face020,Face021]
  Solid = true
FEATURE [Part::Cut] Cut053
  Base = -> Loft002
  Tool = -> Loft005
FEATURE [Part::Cut] Cut054
  Base = -> Cut053
  Tool = -> Loft004
FEATURE [Part::Cut] Cut055
  Base = -> Cut054
  Tool = -> Loft003
FEATURE [Part::Loft] Loft006
  Closed = false
  MaxDegree = 5
  Ruled = false
  Sections = -> [Face008,Face009]
  Solid = true
FEATURE [Part::Loft] Loft007
  Closed = false
  MaxDegree = 5
  Ruled = false
  Sections = -> [Face010,Face011]
  Solid = true
FEATURE [Part::Loft] Loft008
  Closed = false
  MaxDegree = 5
  Ruled = false
  Sections = -> [Face018,Face019]
  Solid = true
FEATURE [Part::Loft] Loft009
  Closed = false
  MaxDegree = 5
  Ruled = false
  Sections = -> [Face016,Face017]
  Solid = true
FEATURE [Part::Cut] Cut056
  Base = -> Cut055
  Tool = -> Loft006
FEATURE [Part::Cut] Cut057
  Base = -> Cut056
  Tool = -> Loft009
FEATURE [Part::Cut] Cut058
  Base = -> Cut057
  Tool = -> Loft008
FEATURE [Part::Cut] Cut059
  Base = -> Cut058
  Tool = -> Loft007
FEATURE [Part::Loft] Loft010
  Closed = false
  MaxDegree = 5
  Ruled = false
  Sections = -> [Face012,Face013]
  Solid = true
FEATURE [Part::Loft] Loft011
  Closed = false
  MaxDegree = 5
  Ruled = false
  Sections = -> [Face014,Face015]
  Solid = true
FEATURE [Part::Cut] Cut060
  Base = -> Cut059
  Tool = -> Loft010
FEATURE [Part::Cut] Cut061
  Base = -> Cut060
  Tool = -> Loft011
FEATURE [Part::Feature] Face024
  shape: bbox 11.4 x 10.93 x 2e-07 mm, 1 faces, 0 solids (baked)
FEATURE [Part::Feature] Face025
  shape: bbox 11.4 x 10.93 x 2e-07 mm, 1 faces, 0 solids (baked)
FEATURE [Part::Feature] Face026 .. Face029  x4 (patterned run collapsed; names and placements below)
  shape: bbox 10.82 x 10.76 x 2e-07 mm, 1 faces, 0 solids (baked)
FEATURE [Part::Feature] Face030
  shape: bbox 11.4 x 10.93 x 2e-07 mm, 1 faces, 0 solids (baked)
FEATURE [Part::Feature] Face031
  shape: bbox 11.4 x 10.93 x 2e-07 mm, 1 faces, 0 solids (baked)
FEATURE [Part::Loft] Loft012
  Closed = false
  MaxDegree = 5
  Ruled = false
  Sections = -> [Face024,Face025]
  Solid = true
FEATURE [Part::Loft] Loft013
  Closed = false
  MaxDegree = 5
  Ruled = false
  Sections = -> [Face026,Face027]
  Solid = true
FEATURE [Part::Loft] Loft014
  Closed = false
  MaxDegree = 5
  Ruled = false
  Sections = -> [Face028,Face029]
  Solid = true
FEATURE [Part::Loft] Loft015
  Closed = false
  MaxDegree = 5
  Ruled = false
  Sections = -> [Face030,Face031]
  Solid = true
FEATURE [Part::Cut] Cut062
  Base = -> Cut061
  Tool = -> Loft012
FEATURE [Part::Cut] Cut063
  Base = -> Cut062
  Tool = -> Loft015
FEATURE [Part::Cut] Cut064
  Base = -> Cut063
  Tool = -> Loft014
FEATURE [Part::Cut] Cut065  label="Main_Buttons_Retainer_Final_1"
  Base = -> Cut064
  Tool = -> Loft013
FEATURE [Part::Cut] Cut066
  Base = -> Fusion040
  Tool = -> Cylinder050
FEATURE [Part::Fillet] Fillet020
  Base = -> Cut066
  Edges = 2 edges r=2: [Edge19,Edge27]
  Placement = pos=(86,0,0) rot=(0,0,1;0rad)
FEATURE [Part::Cut] Cut067
  Base = -> Fusion041
  Tool = -> Cylinder042
FEATURE [Part::Fillet] Fillet021
  Base = -> Cut067
  Edges = 2 edges r=2: [Edge3,Edge16]
  Placement = pos=(86,0,0) rot=(0,0,1;0rad)
FEATURE [Part::Cut] Cut068
  Base = -> Fusion042
  Tool = -> Cylinder051
FEATURE [Part::Fillet] Fillet022
  Base = -> Cut068
  Edges = 2 edges r=2: [Edge19,Edge27]
  Placement = pos=(86,0,0) rot=(0,0,1;0rad)
FEATURE [Part::Cut] Cut069
  Base = -> Fusion039
  Tool = -> Cylinder049
FEATURE [Part::Fillet] Fillet023
  Base = -> Cut069
  Edges = 2 edges r=2: [Edge14,Edge28]
  Placement = pos=(86,0,0) rot=(0,0,1;0rad)
FEATURE [Part::Box] Box114  label="Cube104"
  AttacherType = Attacher::AttachEngine3D
  Height = 1.5
  Length = 2
  Placement = pos=(105,29,9) rot=(0,0,1;0rad)
  Width = 2
FEATURE [Part::Cut] Cut070  label="Main_Buttons_Retainer_Final"
  Base = -> Cut065
  Tool = -> Box114
FEATURE [App::DocumentObjectGroup] Group008  label="Main_Buttons_Retainer"
  Group = -> [Fusion019,Cut070]
FEATURE [Part::MultiFuse] Fusion044
  Shapes = -> [Cut041,Fillet023,Fillet022,Fillet021,Fillet020]
FEATURE [Part::Box] Box115  label="Cube105"
  AttacherType = Attacher::AttachEngine3D
  Height = 10
  Length = 10
  Placement = pos=(77.4,9,0) rot=(0,0,1;0rad)
  Width = 10
FEATURE [Part::Box] Box116  label="Cube106"
  AttacherType = Attacher::AttachEngine3D
  Height = 10
  Length = 10
  Placement = pos=(117.3,9,0) rot=(0,0,1;0rad)
  Width = 10
FEATURE [Part::Box] Box117  label="Cube107"
  AttacherType = Attacher::AttachEngine3D
  Height = 10
  Length = 10
  Placement = pos=(97.4,28.4,0) rot=(0,0,1;0rad)
  Width = 10
FEATURE [Part::Box] Box118  label="Cube108"
  AttacherType = Attacher::AttachEngine3D
  Height = 10
  Length = 10
  Placement = pos=(97.4,-10.4,0) rot=(0,0,1;0rad)
  Width = 10
FEATURE [Part::Cut] Cut071  label="Button_4"
  Base = -> Fusion016
  Tool = -> Box115
FEATURE [Part::Cut] Cut072  label="Button_2"
  Base = -> Fusion014
  Tool = -> Box116
FEATURE [Part::Cut] Cut073  label="Button_1"
  Base = -> Fusion013
  Tool = -> Box117
FEATURE [Part::Cut] Cut074  label="Button_3"
  Base = -> Fusion015
  Tool = -> Box118
FEATURE [App::DocumentObjectGroup] Group010  label="Dpad"
  Group = -> [Fusion006]
FEATURE [Part::Box] Box119  label="Cube109"
  AttacherType = Attacher::AttachEngine3D
  Height = 11
  Length = 15
  Placement = pos=(27,-12,-17) rot=(0,0,1;0rad)
  Width = 51
FEATURE [Part::Box] Box120  label="Cube110"
  AttacherType = Attacher::AttachEngine3D
  Height = 11
  Length = 15
  Placement = pos=(77,-12,-17) rot=(0,0,1;0rad)
  Width = 51
FEATURE [Part::Cut] Cut075
  Base = -> Cut023
  Tool = -> Box119
FEATURE [Part::Box] Box121  label="Main_PCB_Support_3"
  AttacherType = Attacher::AttachEngine3D
  Height = 7
  Length = 2.5
  Placement = pos=(27.5,-5,-13) rot=(0,0,1;0rad)
  Width = 36
FEATURE [Part::Fillet] Fillet024  label="Left_Handle_Right_Side"
  Base = -> Cut075
  Edges = 2 edges r=2: [Edge12,Edge17]
FEATURE [Part::Cut] Cut076
  Base = -> Cut022
  Tool = -> Box120
FEATURE [Part::Fillet] Fillet025  label="Right_Handle_Left_Side"
  Base = -> Cut076
  Edges = 2 edges r=2: [Edge10,Edge14]
FEATURE [App::DocumentObjectGroup] Group002  label="Handles"
  Group = -> [Edge,Cut018,Common,Cut020,Common001,Fillet025,Fillet024]
FEATURE [Part::Box] Box122  label="Cube112"
  AttacherType = Attacher::AttachEngine3D
  Height = 4
  Length = 2.5
  Placement = pos=(27.5,-5,-19) rot=(0,0,1;0rad)
  Width = 36
FEATURE [Part::Box] Box123  label="Cube113"
  AttacherType = Attacher::AttachEngine3D
  Height = 2
  Length = 1
  Placement = pos=(27.5,-4,-15) rot=(0,0,1;0rad)
  Width = 35
FEATURE [Part::Box] Box124  label="Main_PCB_Support_2"
  AttacherType = Attacher::AttachEngine3D
  Height = 7
  Length = 2.5
  Placement = pos=(89,-5,-13) rot=(0,0,1;0rad)
  Width = 36
FEATURE [Part::Box] Box125  label="Cube115"
  AttacherType = Attacher::AttachEngine3D
  Height = 2
  Length = 1
  Placement = pos=(90.5,-4,-15) rot=(0,0,1;0rad)
  Width = 35
FEATURE [Part::Box] Box126  label="Cube116"
  AttacherType = Attacher::AttachEngine3D
  Height = 4
  Length = 2.5
  Placement = pos=(89,-5,-19) rot=(0,0,1;0rad)
  Width = 36
FEATURE [Part::Box] Box128  label="Cube118"
  AttacherType = Attacher::AttachEngine3D
  Height = 2
  Length = 64
  Placement = pos=(27.5,-5,-15) rot=(0,0,1;0rad)
  Width = 1
FEATURE [Part::Box] Box129  label="Cube119"
  AttacherType = Attacher::AttachEngine3D
  Height = 2
  Length = 59
  Placement = pos=(30,-5,-19) rot=(0,0,1;0rad)
  Width = 36
FEATURE [Part::Box] Box130  label="Cube120"
  AttacherType = Attacher::AttachEngine3D
  Height = 2
  Length = 20
  Placement = pos=(49.5,19,-19) rot=(0,0,1;0rad)
  Width = 12
FEATURE [Part::Box] Box131  label="Cube121"
  AttacherType = Attacher::AttachEngine3D
  Height = 2
  Length = 59
  Placement = pos=(30,-5,-17) rot=(0,0,1;0rad)
  Width = 2
FEATURE [Part::Cylinder] Cylinder054  label="Cylinder135"
  Angle = 360
  AttacherType = Attacher::AttachEngine3D
  Height = 2
  Placement = pos=(39,20,-19) rot=(0,0,1;0rad)
  Radius = 8
FEATURE [Part::Cylinder] Cylinder055  label="Cylinder136"
  Angle = 360
  AttacherType = Attacher::AttachEngine3D
  Height = 2
  Placement = pos=(80,20,-19) rot=(0,0,1;0rad)
  Radius = 8
FEATURE [Part::Cylinder] Cylinder056  label="Cylinder137"
  Angle = 360
  AttacherType = Attacher::AttachEngine3D
  Height = 2
  Placement = pos=(80,4,-19) rot=(0,0,1;0rad)
  Radius = 6
FEATURE [Part::Cylinder] Cylinder057  label="Cylinder138"
  Angle = 360
  AttacherType = Attacher::AttachEngine3D
  Height = 2
  Placement = pos=(39,4,-19) rot=(0,0,1;0rad)
  Radius = 6
FEATURE [Part::Cut] Cut077
  Base = -> Box129
  Tool = -> Box130
FEATURE [Part::Cut] Cut078
  Base = -> Cut077
  Tool = -> Cylinder056
FEATURE [Part::Cut] Cut079
  Base = -> Cut078
  Tool = -> Cylinder057
FEATURE [Part::Cut] Cut080
  Base = -> Cut079
  Tool = -> Cylinder054
FEATURE [Part::Cut] Cut081
  Base = -> Cut080
  Tool = -> Cylinder055
FEATURE [Part::MultiFuse] Fusion045
  Shapes = -> [Box122,Box123,Box126,Box128,Box131,Box125,Cut081]
FEATURE [Part::Fillet] Fillet026
  Base = -> Fusion045
  Edges = 2 edges r=1.9: [Edge2,Edge71]
FEATURE [Part::Fillet] Fillet027  label="Main_PCB_Support_1"
  Base = -> Fillet026
  Edges = 2 edges r=9: [Edge37,Edge90]
FEATURE [App::DocumentObjectGroup] Group011  label="Main_PCB_Support"
  Group = -> [Box124,Box121,Fillet027]
FEATURE [Part::Box] Box132  label="Cube_001"
  AttacherType = Attacher::AttachEngine3D
  Height = 3
  Length = 63
  Placement = pos=(28,-17,-6) rot=(0,0,1;0rad)
  Width = 19
FEATURE [Part::Fillet] Fillet028
  Base = -> Box132
  Edges = 2 edges r=5: [Edge1,Edge5]
FEATURE [Part::Box] Box133  label="Cube122"
  AttacherType = Attacher::AttachEngine3D
  Height = 3
  Length = 43.5
  Placement = pos=(37.5,-3,-3) rot=(0,0,1;0rad)
  Width = 3
FEATURE [Part::Box] Box134  label="Cube123"
  AttacherType = Attacher::AttachEngine3D
  Height = 3
  Length = 3
  Placement = pos=(34.5,-17,-3) rot=(0,0,1;0rad)
  Width = 17
FEATURE [Part::Box] Box135  label="Cube124"
  AttacherType = Attacher::AttachEngine3D
  Height = 3
  Length = 3
  Placement = pos=(81,-17,-3) rot=(0,0,1;0rad)
  Width = 17
FEATURE [Part::Box] Box136  label="Cube125"
  AttacherType = Attacher::AttachEngine3D
  Height = 3
  Length = 7
  Placement = pos=(55.5,-17,-3) rot=(0,0,1;0rad)
  Width = 14
FEATURE [Part::Box] Box137  label="Cube126"
  AttacherType = Attacher::AttachEngine3D
  Height = 2
  Length = 5
  Placement = pos=(56.7,-17,0) rot=(0,0,1;0rad)
  Width = 16
FEATURE [Part::Box] Box138  label="Cube127"
  AttacherType = Attacher::AttachEngine3D
  Height = 2
  Length = 47.5
  Placement = pos=(35.5,-1,0) rot=(0,0,1;0rad)
  Width = 1
FEATURE [Part::Box] Box139  label="Cube128"
  AttacherType = Attacher::AttachEngine3D
  Height = 2
  Length = 7
  Placement = pos=(55.5,-17,2) rot=(0,0,1;0rad)
  Width = 15
FEATURE [Part::Box] Box140  label="Cube129"
  AttacherType = Attacher::AttachEngine3D
  Height = 2
  Length = 1
  Placement = pos=(34.5,-17,0) rot=(0,0,1;0rad)
  Width = 17
FEATURE [Part::Box] Box141  label="Cube130"
  AttacherType = Attacher::AttachEngine3D
  Height = 2
  Length = 1
  Placement = pos=(83,-17,0) rot=(0,0,1;0rad)
  Width = 17
FEATURE [Part::Box] Box142  label="Cube131"
  AttacherType = Attacher::AttachEngine3D
  Height = 2
  Length = 49.5
  Placement = pos=(34.5,-2,2) rot=(0,0,1;0rad)
  Width = 2
FEATURE [Part::Box] Box143  label="Cube132"
  AttacherType = Attacher::AttachEngine3D
  Height = 2
  Length = 3
  Placement = pos=(34.5,-17,2) rot=(0,0,1;0rad)
  Width = 15
FEATURE [Part::Box] Box144  label="Cube133"
  AttacherType = Attacher::AttachEngine3D
  Height = 2
  Length = 3
  Placement = pos=(81,-17,2) rot=(0,0,1;0rad)
  Width = 15
FEATURE [Part::Box] Box145  label="Cube134"
  AttacherType = Attacher::AttachEngine3D
  Height = 1.5
  Length = 11
  Placement = pos=(37,15,-6) rot=(0,0,1;0rad)
  Width = 23
FEATURE [Part::Cylinder] Cylinder058  label="Cylinder139"
  Angle = 360
  AttacherType = Attacher::AttachEngine3D
  Height = 1.54
  Placement = pos=(42.5,33,-6) rot=(0,0,1;0rad)
  Radius = 1.6
FEATURE [Part::Box] Box146  label="Cube135"
  AttacherType = Attacher::AttachEngine3D
  Height = 1.5
  Length = 11
  Placement = pos=(71,15,-6) rot=(0,0,1;0rad)
  Width = 23
FEATURE [Part::Cylinder] Cylinder059  label="Cylinder140"
  Angle = 360
  AttacherType = Attacher::AttachEngine3D
  Height = 1.54
  Placement = pos=(76.5,33,-6) rot=(0,0,1;0rad)
  Radius = 1.6
FEATURE [Part::Fillet] Fillet029
  Base = -> Box145
  Edges = 1 edges r=5: [Edge3]
FEATURE [Part::Fillet] Fillet030
  Base = -> Box146
  Edges = 1 edges r=5: [Edge7]
FEATURE [Part::Cut] Cut082
  Base = -> Fillet029
  Tool = -> Cylinder058
FEATURE [Part::Cut] Cut083
  Base = -> Fillet030
  Tool = -> Cylinder059
FEATURE [Part::Fillet] Fillet031
  Base = -> Cut082
  Edges = 1 edges r=5: [Edge14]
FEATURE [Part::Fillet] Fillet032
  Base = -> Cut083
  Edges = 2 edges r=5: [Edge14,Edge19]
FEATURE [Part::Fillet] Fillet033
  Base = -> Fillet031
  Edges = 1 edges r=5: [Edge16]
FEATURE [Part::MultiFuse] Fusion046
  Shapes = -> [Box133,Box134,Box135,Box136,Box137,Box138,Box140,Box141]
FEATURE [Part::MultiFuse] Fusion047  label="Main_Support_2"
  Shapes = -> [Box139,Box142,Box143,Box144]
FEATURE [Part::Cylinder] Cylinder060  label="Cylinder141"
  Angle = 360
  AttacherType = Attacher::AttachEngine3D
  Height = 3
  Placement = pos=(46.5,-10,-6) rot=(0,0,1;0rad)
  Radius = 5.5
FEATURE [Part::Cylinder] Cylinder061  label="Cylinder142"
  Angle = 360
  AttacherType = Attacher::AttachEngine3D
  Height = 3
  Placement = pos=(71.5,-10,-6) rot=(0,0,1;0rad)
  Radius = 5.5
FEATURE [Part::Cut] Cut084
  Base = -> Fillet028
  Tool = -> Cylinder060
FEATURE [Part::Cut] Cut085
  Base = -> Cut084
  Tool = -> Cylinder061
FEATURE [Part::MultiFuse] Fusion048  label="Main_Support_1"
  Shapes = -> [Fusion043,Fusion044,Fillet032,Fillet033,Fusion046,Cut085]
FEATURE [App::DocumentObjectGroup] Group001  label="Main_Support"
  Group = -> [Fusion048,Fusion047]
FEATURE [Part::Cylinder] Cylinder062  label="Cylinder143"
  Angle = 360
  AttacherType = Attacher::AttachEngine3D
  Height = 3
  Placement = pos=(16.5,14,-6) rot=(0,0,1;0rad)
  Radius = 25.5
FEATURE [Part::Cylinder] Cylinder063  label="Cylinder144"
  Angle = 360
  AttacherType = Attacher::AttachEngine3D
  Height = 3
  Placement = pos=(102,14,-6) rot=(0,0,1;0rad)
  Radius = 25.5
FEATURE [Part::Box] Box147  label="Cube136"
  AttacherType = Attacher::AttachEngine3D
  Height = 1.5
  Length = 45
  Placement = pos=(37,15,-4.5) rot=(0,0,1;0rad)
  Width = 23
FEATURE [Part::Cut] Cut086
  Base = -> Box147
  Tool = -> Cylinder062
FEATURE [Part::Cut] Cut087
  Base = -> Cut086
  Tool = -> Cylinder063
FEATURE [Part::Fillet] Fillet034
  Base = -> Cut087
  Edges = 2 edges r=5: [Edge2,Edge4]
FEATURE [Part::Cylinder] Cylinder064  label="Cylinder145"
  Angle = 360
  AttacherType = Attacher::AttachEngine3D
  Height = 1.5
  Placement = pos=(42.5,33,-4.5) rot=(0,0,1;0rad)
  Radius = 1.6
FEATURE [Part::Cylinder] Cylinder065  label="Cylinder146"
  Angle = 360
  AttacherType = Attacher::AttachEngine3D
  Height = 1.5
  Placement = pos=(76.5,33,-4.5) rot=(0,0,1;0rad)
  Radius = 1.6
FEATURE [Part::Cut] Cut088
  Base = -> Fillet034
  Tool = -> Cylinder064
FEATURE [Part::Cut] Cut089
  Base = -> Cut088
  Tool = -> Cylinder065
FEATURE [Part::Box] Box148  label="Cube137"
  AttacherType = Attacher::AttachEngine3D
  Height = 9
  Length = 3
  Placement = pos=(52.5,29.25,-3) rot=(0,0,1;0rad)
  Width = 6
FEATURE [Part::Box] Box149  label="Cube138"
  AttacherType = Attacher::AttachEngine3D
  Height = 9
  Length = 3
  Placement = pos=(63,29.25,-3) rot=(0,0,1;0rad)
  Width = 6
FEATURE [Part::Box] Box150  label="Cube139"
  AttacherType = Attacher::AttachEngine3D
  Height = 2.3
  Length = 13.5
  Placement = pos=(52.5,29.25,6) rot=(0,0,1;0rad)
  Width = 6
FEATURE [Part::Cylinder] Cylinder066  label="Cylinder147"
  Angle = 360
  AttacherType = Attacher::AttachEngine3D
  Height = 3
  Placement = pos=(59.25,32.25,6) rot=(0,0,1;0rad)
  Radius = 1.6
FEATURE [Part::Box] Box151  label="Cube140"
  AttacherType = Attacher::AttachEngine3D
  Height = 3
  Length = 2
  Placement = pos=(41.5,20,-3) rot=(0,0,1;0rad)
  Width = 10.25
FEATURE [Part::Box] Box152  label="Cube141"
  AttacherType = Attacher::AttachEngine3D
  Height = 3
  Length = 2
  Placement = pos=(75,20,-3) rot=(0,0,1;0rad)
  Width = 10.25
FEATURE [Part::Box] Box153  label="Cube142"
  AttacherType = Attacher::AttachEngine3D
  Height = 2
  Length = 1
  Placement = pos=(41.5,20,0) rot=(0,0,1;0rad)
  Width = 10.25
FEATURE [Part::Box] Box154  label="Cube143"
  AttacherType = Attacher::AttachEngine3D
  Height = 2
  Length = 1
  Placement = pos=(76,20,0) rot=(0,0,1;0rad)
  Width = 10.25
FEATURE [Part::Box] Box155  label="Cube144"
  AttacherType = Attacher::AttachEngine3D
  Height = 3
  Length = 7.5
  Placement = pos=(55.5,28.5,-3) rot=(0,0,1;0rad)
  Width = 5.5
FEATURE [Part::Box] Box156  label="Cube145"
  AttacherType = Attacher::AttachEngine3D
  Height = 3
  Length = 9
  Placement = pos=(43.5,28.25,-3) rot=(0,0,1;0rad)
  Width = 2
FEATURE [Part::Box] Box157  label="Cube146"
  AttacherType = Attacher::AttachEngine3D
  Height = 3
  Length = 9
  Placement = pos=(66,28.25,-3) rot=(0,0,1;0rad)
  Width = 2
FEATURE [Part::Box] Box158  label="Cube147"
  AttacherType = Attacher::AttachEngine3D
  Height = 2
  Length = 10
  Placement = pos=(66,29.25,0) rot=(0,0,1;0rad)
  Width = 1
FEATURE [Part::Box] Box159  label="Cube148"
  AttacherType = Attacher::AttachEngine3D
  Height = 2
  Length = 10
  Placement = pos=(42.5,29.25,0) rot=(0,0,1;0rad)
  Width = 1
FEATURE [Part::Fillet] Fillet035
  Base = -> Box150
  Edges = 2 edges r=2: [Edge2,Edge6]
FEATURE [Part::Cut] Cut090
  Base = -> Fillet035
  Tool = -> Cylinder066
FEATURE [Part::MultiFuse] Fusion049  label="Middle_Buttons_Support_1"
  Shapes = -> [Cut089,Box148,Box149,Box151,Box152,Box153,Box154,Box155,Box156,Box157,Box158,Box159,Cut090]
FEATURE [Part::Box] Box160  label="Cube149"
  AttacherType = Attacher::AttachEngine3D
  Height = 2
  Length = 2
  Placement = pos=(41.5,20,2) rot=(0,0,1;0rad)
  Width = 10.25
FEATURE [Part::Box] Box161  label="Cube150"
  AttacherType = Attacher::AttachEngine3D
  Height = 2
  Length = 9
  Placement = pos=(66,28.25,2) rot=(0,0,1;0rad)
  Width = 2
FEATURE [Part::Box] Box162  label="Cube151"
  AttacherType = Attacher::AttachEngine3D
  Height = 2
  Length = 9
  Placement = pos=(43.5,28.25,2) rot=(0,0,1;0rad)
  Width = 2
FEATURE [Part::Box] Box163  label="Cube152"
  AttacherType = Attacher::AttachEngine3D
  Height = 2
  Length = 2
  Placement = pos=(75,20,2) rot=(0,0,1;0rad)
  Width = 10.25
FEATURE [Part::MultiFuse] Fusion050  label="Middle_Buttons_Support_2"
  Shapes = -> [Box160,Box162]
FEATURE [Part::MultiFuse] Fusion051  label="Middle_Buttons_Support_3"
  Shapes = -> [Box161,Box163]
FEATURE [App::DocumentObjectGroup] Group012  label="Middle_Buttons_Support"
  Group = -> [Fusion049,Fusion050,Fusion051]
FEATURE [Part::Box] Box164  label="Cube153"
  AttacherType = Attacher::AttachEngine3D
  Height = 11
  Length = 17
  Placement = pos=(38,-19,-12) rot=(0,0,1;0rad)
  Width = 2
FEATURE [Part::Box] Box165  label="Cube154"
  AttacherType = Attacher::AttachEngine3D
  Height = 1.5
  Length = 4
  Placement = pos=(39,-17,-2.5) rot=(0,0,1;0rad)
  Width = 2
FEATURE [Part::Box] Box166  label="Cube155"
  AttacherType = Attacher::AttachEngine3D
  Height = 1.5
  Length = 4
  Placement = pos=(39,-17,-8) rot=(0,0,1;0rad)
  Width = 2
FEATURE [Part::Box] Box167  label="Cube156"
  AttacherType = Attacher::AttachEngine3D
  Height = 1.5
  Length = 4
  Placement = pos=(50,-17,-8) rot=(0,0,1;0rad)
  Width = 2
FEATURE [Part::Box] Box168  label="Cube157"
  AttacherType = Attacher::AttachEngine3D
  Height = 1.5
  Length = 4
  Placement = pos=(50,-17,-2.5) rot=(0,0,1;0rad)
  Width = 2
FEATURE [Part::Cylinder] Cylinder067  label="Cylinder148"
  Angle = 360
  AttacherType = Attacher::AttachEngine3D
  Height = 2
  Placement = pos=(46.5,-17,-9) rot=(1,0,0;1.5708rad)
  Radius = 1.6
FEATURE [Part::Fillet] Fillet036
  Base = -> Box164
  Edges = 2 edges r=5: [Edge4,Edge8]
FEATURE [Part::Box] Box169  label="Cube158"
  AttacherType = Attacher::AttachEngine3D
  Height = 11
  Length = 17
  Placement = pos=(63.5,-19,-12) rot=(0,0,1;0rad)
  Width = 2
FEATURE [Part::Cylinder] Cylinder068  label="Cylinder149"
  Angle = 360
  AttacherType = Attacher::AttachEngine3D
  Height = 2
  Placement = pos=(72,-17,-9) rot=(1,0,0;1.5708rad)
  Radius = 1.6
FEATURE [Part::Box] Box170  label="Cube159"
  AttacherType = Attacher::AttachEngine3D
  Height = 1.5
  Length = 4
  Placement = pos=(75.5,-17,-2.5) rot=(0,0,1;0rad)
  Width = 2
FEATURE [Part::Box] Box171  label="Cube160"
  AttacherType = Attacher::AttachEngine3D
  Height = 1.5
  Length = 4
  Placement = pos=(64.5,-17,-2.5) rot=(0,0,1;0rad)
  Width = 2
FEATURE [Part::Box] Box172  label="Cube161"
  AttacherType = Attacher::AttachEngine3D
  Height = 1.5
  Length = 4
  Placement = pos=(75.5,-17,-8) rot=(0,0,1;0rad)
  Width = 2
FEATURE [Part::Box] Box174  label="Cube163"
  AttacherType = Attacher::AttachEngine3D
  Height = 8
  Length = 10
  Placement = pos=(79,31,-25) rot=(0,0,1;0rad)
  Width = 2
FEATURE [Part::Box] Box175  label="Cube164"
  AttacherType = Attacher::AttachEngine3D
  Height = 1.5
  Length = 2
  Placement = pos=(87,29,-20.5) rot=(0,0,1;0rad)
  Width = 2
FEATURE [Part::Box] Box176  label="Cube165"
  AttacherType = Attacher::AttachEngine3D
  Height = 1.5
  Length = 2
  Placement = pos=(79,29,-20.5) rot=(0,0,1;0rad)
  Width = 2
FEATURE [Part::Cylinder] Cylinder069  label="Cylinder150"
  Angle = 360
  AttacherType = Attacher::AttachEngine3D
  Height = 2
  Placement = pos=(84,33,-22) rot=(1,0,0;1.5708rad)
  Radius = 1.6
FEATURE [Part::Fillet] Fillet037
  Base = -> Box169
  Edges = 2 edges r=5: [Edge4,Edge8]
FEATURE [Part::Cut] Cut091
  Base = -> Fillet037
  Tool = -> Cylinder068
FEATURE [Part::Cut] Cut092
  Base = -> Fillet036
  Tool = -> Cylinder067
FEATURE [Part::MultiFuse] Fusion052  label="Analog_Latch_1"
  Shapes = -> [Box168,Cut092,Box165,Box167,Box166]
FEATURE [Part::Box] Box177  label="Cube166"
  AttacherType = Attacher::AttachEngine3D
  Height = 1.5
  Length = 4
  Placement = pos=(64.5,-17,-8) rot=(0,0,1;0rad)
  Width = 2
FEATURE [Part::MultiFuse] Fusion053  label="Analog_Latch_2"
  Shapes = -> [Cut091,Box177,Box172,Box171,Box170]
FEATURE [Part::Box] Box178  label="Cube167"
  AttacherType = Attacher::AttachEngine3D
  Height = 8
  Length = 10
  Placement = pos=(30,31,-25) rot=(0,0,1;0rad)
  Width = 2
FEATURE [Part::Cylinder] Cylinder070  label="Cylinder151"
  Angle = 360
  AttacherType = Attacher::AttachEngine3D
  Height = 2
  Placement = pos=(35,33,-22) rot=(1,0,0;1.5708rad)
  Radius = 1.6
FEATURE [Part::Box] Box179  label="Cube168"
  AttacherType = Attacher::AttachEngine3D
  Height = 1.5
  Length = 2
  Placement = pos=(38,29,-20.5) rot=(0,0,1;0rad)
  Width = 2
FEATURE [Part::Box] Box180  label="Cube169"
  AttacherType = Attacher::AttachEngine3D
  Height = 1.5
  Length = 2
  Placement = pos=(30,29,-20.5) rot=(0,0,1;0rad)
  Width = 2
FEATURE [Part::Cut] Cut093
  Base = -> Box174
  Tool = -> Cylinder069
FEATURE [Part::Cut] Cut094
  Base = -> Box178
  Tool = -> Cylinder070
FEATURE [Part::Fillet] Fillet038
  Base = -> Cut093
  Edges = 2 edges r=3: [Edge4,Edge14]
FEATURE [Part::Fillet] Fillet039
  Base = -> Cut094
  Edges = 2 edges r=3: [Edge4,Edge14]
FEATURE [Part::MultiFuse] Fusion054  label="Main_PCB_Latch_1"
  Shapes = -> [Box179,Fillet039,Box180]
FEATURE [Part::MultiFuse] Fusion055  label="Main_PCB_Latch_2"
  Shapes = -> [Fillet038,Box176,Box175]
FEATURE [Part::Box] Box181  label="Cube170"
  AttacherType = Attacher::AttachEngine3D
  Height = 12
  Length = 10
  Placement = pos=(79,33,-25) rot=(0,0,1;0rad)
  Width = 2
FEATURE [Part::Box] Box182  label="Cube171"
  AttacherType = Attacher::AttachEngine3D
  Height = 12
  Length = 10
  Placement = pos=(30,33,-25) rot=(0,0,1;0rad)
  Width = 2
FEATURE [Part::Box] Box183  label="Cube172"
  AttacherType = Attacher::AttachEngine3D
  Height = 3
  Length = 10
  Placement = pos=(79,29.5,-16) rot=(0,0,1;0rad)
  Width = 3.5
FEATURE [Part::Box] Box184  label="Cube173"
  AttacherType = Attacher::AttachEngine3D
  Height = 3
  Length = 10
  Placement = pos=(30,29.5,-16) rot=(0,0,1;0rad)
  Width = 3.5
FEATURE [Part::Cylinder] Cylinder071  label="Cylinder152"
  Angle = 360
  AttacherType = Attacher::AttachEngine3D
  Height = 2
  Placement = pos=(35,35,-22) rot=(1,0,0;1.5708rad)
  Radius = 1.6
FEATURE [Part::Cylinder] Cylinder072  label="Cylinder153"
  Angle = 360
  AttacherType = Attacher::AttachEngine3D
  Height = 2
  Placement = pos=(84,35,-22) rot=(1,0,0;1.5708rad)
  Radius = 1.6
FEATURE [Part::Cut] Cut095
  Base = -> Box181
  Tool = -> Cylinder072
FEATURE [Part::Cut] Cut096
  Base = -> Box182
  Tool = -> Cylinder071
FEATURE [Part::Fillet] Fillet040
  Base = -> Cut095
  Edges = 2 edges r=3: [Edge4,Edge14]
FEATURE [Part::Fillet] Fillet041
  Base = -> Cut096
  Edges = 2 edges r=3: [Edge4,Edge14]
FEATURE [Part::MultiFuse] Fusion056  label="Main_PCB_Latch_3"
  Shapes = -> [Fillet040,Box183]
FEATURE [Part::MultiFuse] Fusion057  label="Main_PCB_Latch_4"
  Shapes = -> [Fillet041,Box184]
FEATURE [Part::Box] Box185  label="Cube174"
  AttacherType = Attacher::AttachEngine3D
  Height = 14
  Length = 17
  Placement = pos=(63.5,-21,-12) rot=(0,0,1;0rad)
  Width = 2
FEATURE [Part::Cylinder] Cylinder073  label="Cylinder154"
  Angle = 360
  AttacherType = Attacher::AttachEngine3D
  Height = 2
  Placement = pos=(72,-19,-9) rot=(1,0,0;1.5708rad)
  Radius = 1.6
FEATURE [Part::Box] Box186  label="Cube175"
  AttacherType = Attacher::AttachEngine3D
  Height = 2.5
  Length = 17
  Placement = pos=(63.5,-19,-0.5) rot=(0,0,1;0rad)
  Width = 2.5
FEATURE [Part::Box] Box187  label="Cube176"
  AttacherType = Attacher::AttachEngine3D
  Height = 2.5
  Length = 17
  Placement = pos=(38,-19,-0.5) rot=(0,0,1;0rad)
  Width = 2.5
FEATURE [Part::Box] Box188  label="Cube177"
  AttacherType = Attacher::AttachEngine3D
  Height = 14
  Length = 17
  Placement = pos=(38,-21,-12) rot=(0,0,1;0rad)
  Width = 2
FEATURE [Part::Cylinder] Cylinder074  label="Cylinder155"
  Angle = 360
  AttacherType = Attacher::AttachEngine3D
  Height = 2
  Placement = pos=(46.5,-19,-9) rot=(1,0,0;1.5708rad)
  Radius = 1.6
FEATURE [Part::Cut] Cut097
  Base = -> Box188
  Tool = -> Cylinder074
FEATURE [Part::Cut] Cut098
  Base = -> Box185
  Tool = -> Cylinder073
FEATURE [Part::Fillet] Fillet042
  Base = -> Cut097
  Edges = 2 edges r=5: [Edge4,Edge14]
FEATURE [Part::Fillet] Fillet043
  Base = -> Cut098
  Edges = 2 edges r=5: [Edge4,Edge14]
FEATURE [Part::MultiFuse] Fusion058  label="Analog_Latch_3"
  Shapes = -> [Box186,Fillet043]
FEATURE [Part::MultiFuse] Fusion059  label="Analog_Latch_4"
  Shapes = -> [Box187,Fillet042]
FEATURE [Part::Box] Box189  label="Cube178"
  AttacherType = Attacher::AttachEngine3D
  Height = 2.3
  Length = 10.5
  Placement = pos=(42.5,11,6) rot=(0,0,1;0rad)
  Width = 8
FEATURE [Part::Box] Box190  label="Cube179"
  AttacherType = Attacher::AttachEngine3D
  Height = 2.3
  Length = 10.5
  Placement = pos=(65,11,6) rot=(0,0,1;0rad)
  Width = 8
FEATURE [Part::Box] Box191  label="Cube180"
  AttacherType = Attacher::AttachEngine3D
  Height = 9
  Length = 10
  Placement = pos=(54,13,-10) rot=(0,0,1;0rad)
  Width = 2
FEATURE [Part::Cylinder] Cylinder075  label="Cylinder156"
  Angle = 360
  AttacherType = Attacher::AttachEngine3D
  Height = 2
  Placement = pos=(59,15,-7) rot=(1,0,0;1.5708rad)
  Radius = 1.6
FEATURE [Part::Box] Box193  label="Cube182"
  AttacherType = Attacher::AttachEngine3D
  Height = 1.5
  Length = 10
  Placement = pos=(54,15,-2.5) rot=(0,0,1;0rad)
  Width = 2
FEATURE [Part::Fillet] Fillet044
  Base = -> Box191
  Edges = 2 edges r=3: [Edge4,Edge8]
FEATURE [Part::Cut] Cut099
  Base = -> Fillet044
  Tool = -> Cylinder075
FEATURE [Part::MultiFuse] Fusion060  label="Middle_Latch_1"
  Shapes = -> [Cut099,Box193]
FEATURE [Part::Box] Box194  label="Cube183"
  AttacherType = Attacher::AttachEngine3D
  Height = 9
  Length = 33
  Placement = pos=(42.5,11,-10) rot=(0,0,1;0rad)
  Width = 2
FEATURE [Part::Cylinder] Cylinder076  label="Cylinder157"
  Angle = 360
  AttacherType = Attacher::AttachEngine3D
  Height = 2
  Placement = pos=(59,13,-7) rot=(1,0,0;1.5708rad)
  Radius = 1.6
FEATURE [Part::Box] Box195  label="Cube184"
  AttacherType = Attacher::AttachEngine3D
  Height = 9
  Length = 2
  Placement = pos=(65,11,-3) rot=(0,0,1;0rad)
  Width = 8
FEATURE [Part::Box] Box196  label="Cube185"
  AttacherType = Attacher::AttachEngine3D
  Height = 9
  Length = 2
  Placement = pos=(73.5,11,-3) rot=(0,0,1;0rad)
  Width = 8
FEATURE [Part::Box] Box197  label="Cube186"
  AttacherType = Attacher::AttachEngine3D
  Height = 3
  Length = 6.5
  Placement = pos=(67,11,-3) rot=(0,0,1;0rad)
  Width = 9
FEATURE [Part::Box] Box198  label="Cube187"
  AttacherType = Attacher::AttachEngine3D
  Height = 9
  Length = 2
  Placement = pos=(42.5,11,-3) rot=(0,0,1;0rad)
  Width = 8
FEATURE [Part::Box] Box199  label="Cube188"
  AttacherType = Attacher::AttachEngine3D
  Height = 9
  Length = 2
  Placement = pos=(51,11,-3) rot=(0,0,1;0rad)
  Width = 8
FEATURE [Part::Box] Box200  label="Cube189"
  AttacherType = Attacher::AttachEngine3D
  Height = 3
  Length = 6.5
  Placement = pos=(44.5,11,-3) rot=(0,0,1;0rad)
  Width = 9
FEATURE [Part::Cylinder] Cylinder077  label="Cylinder158"
  Angle = 360
  AttacherType = Attacher::AttachEngine3D
  Height = 2.3
  Placement = pos=(47.75,15,6) rot=(0,0,1;0rad)
  Radius = 1.6
FEATURE [Part::Cylinder] Cylinder078  label="Cylinder159"
  Angle = 360
  AttacherType = Attacher::AttachEngine3D
  Height = 2.3
  Placement = pos=(70.25,15,6) rot=(0,0,1;0rad)
  Radius = 1.6
FEATURE [Part::Cut] Cut100
  Base = -> Box189
  Tool = -> Cylinder077
FEATURE [Part::Cut] Cut101
  Base = -> Box190
  Tool = -> Cylinder078
FEATURE [Part::Cut] Cut102
  Base = -> Box194
  Tool = -> Cylinder076
FEATURE [Part::Fillet] Fillet045
  Base = -> Cut101
  Edges = 2 edges r=2: [Edge2,Edge10]
FEATURE [Part::Fillet] Fillet046
  Base = -> Cut100
  Edges = 2 edges r=2: [Edge2,Edge10]
FEATURE [Part::Fillet] Fillet047
  Base = -> Cut102
  Edges = 2 edges r=5: [Edge4,Edge14]
FEATURE [Part::MultiFuse] Fusion061  label="Middle_Latch_2"
  Shapes = -> [Fillet047,Fillet046,Fillet045,Box200,Box199,Box198,Box197,Box196,Box195]
FEATURE [Part::Box] Box201  label="Cube190"
  AttacherType = Attacher::AttachEngine3D
  Height = 5
  Length = 13
  Placement = pos=(44,20,6.3) rot=(0,0,1;0rad)
  Width = 8
FEATURE [Part::Box] Box202  label="Cube191"
  AttacherType = Attacher::AttachEngine3D
  Height = 5
  Length = 13
  Placement = pos=(61.5,20,6.3) rot=(0,0,1;0rad)
  Width = 8
FEATURE [Part::Box] Box203  label="Cube192"
  AttacherType = Attacher::AttachEngine3D
  Height = 1.5
  Length = 15.5
  Placement = pos=(42.75,19.25,6.3) rot=(0,0,1;0rad)
  Width = 9.5
FEATURE [Part::Box] Box204  label="Cube193"
  AttacherType = Attacher::AttachEngine3D
  Height = 1.5
  Length = 15.5
  Placement = pos=(60.25,19.25,6.3) rot=(0,0,1;0rad)
  Width = 9.5
FEATURE [Part::Fillet] Fillet048
  Base = -> Box201
  Edges = 4 edges r=1: [Edge2,Edge6,Edge10,Edge12]
FEATURE [Part::Fillet] Fillet049
  Base = -> Box202
  Edges = 4 edges r=1: [Edge2,Edge6,Edge10,Edge12]
FEATURE [Part::MultiFuse] Fusion062  label="Middle_Button_1"
  Shapes = -> [Box203,Fillet048]
FEATURE [Part::MultiFuse] Fusion063  label="Middle_Button_2"
  Shapes = -> [Box204,Fillet049]
FEATURE [Part::Box] Box205  label="Cube194"
  AttacherType = Attacher::AttachEngine3D
  Height = 1.5
  Length = 36
  Placement = pos=(41,18,8.3) rot=(0,0,1;0rad)
  Width = 12
FEATURE [Part::Cylinder] Cylinder079  label="Cylinder160"
  Angle = 360
  AttacherType = Attacher::AttachEngine3D
  Height = 1.5
  Placement = pos=(47.75,15,8.3) rot=(0,0,1;0rad)
  Radius = 4
FEATURE [Part::Cylinder] Cylinder080  label="Cylinder161"
  Angle = 360
  AttacherType = Attacher::AttachEngine3D
  Height = 1.5
  Placement = pos=(47.75,15,8.3) rot=(0,0,1;0rad)
  Radius = 1.6
FEATURE [Part::Cylinder] Cylinder081  label="Cylinder162"
  Angle = 360
  AttacherType = Attacher::AttachEngine3D
  Height = 1.5
  Placement = pos=(70.25,15,8.3) rot=(0,0,1;0rad)
  Radius = 1.6
FEATURE [Part::Cylinder] Cylinder082  label="Cylinder163"
  Angle = 360
  AttacherType = Attacher::AttachEngine3D
  Height = 1.5
  Placement = pos=(70.25,15,8.3) rot=(0,0,1;0rad)
  Radius = 4
FEATURE [Part::Cylinder] Cylinder083  label="Cylinder164"
  Angle = 360
  AttacherType = Attacher::AttachEngine3D
  Height = 1.5
  Placement = pos=(59.25,32.25,8.3) rot=(0,0,1;0rad)
  Radius = 1.6
FEATURE [Part::Cylinder] Cylinder084  label="Cylinder165"
  Angle = 360
  AttacherType = Attacher::AttachEngine3D
  Height = 1.5
  Placement = pos=(59.25,32.25,8.3) rot=(0,0,1;0rad)
  Radius = 4
FEATURE [Part::Cut] Cut103
  Base = -> Cylinder079
  Tool = -> Cylinder080
FEATURE [Part::Cut] Cut104
  Base = -> Cylinder082
  Tool = -> Cylinder081
FEATURE [Part::Cut] Cut105
  Base = -> Cylinder084
  Tool = -> Cylinder083
FEATURE [Part::Box] Box206  label="Cube195"
  AttacherType = Attacher::AttachEngine3D
  Height = 1.5
  Length = 14
  Placement = pos=(43.5,19.5,8.3) rot=(0,0,1;0rad)
  Width = 9
FEATURE [Part::Box] Box207  label="Cube196"
  AttacherType = Attacher::AttachEngine3D
  Height = 1.5
  Length = 14
  Placement = pos=(61,19.5,8.3) rot=(0,0,1;0rad)
  Width = 9
FEATURE [Part::Cut] Cut106
  Base = -> Box205
  Tool = -> Box206
FEATURE [Part::Cut] Cut107
  Base = -> Cut106
  Tool = -> Box207
FEATURE [Part::Fillet] Fillet050
  Base = -> Cut107
  Edges = 4 edges r=2: [Edge1,Edge3,Edge6,Edge19]
FEATURE [Part::MultiFuse] Fusion064  label="Middle_Buttons_Retainer_1"
  Shapes = -> [Cut103,Cut104,Cut105,Fillet050]
FEATURE [App::DocumentObjectGroup] Group014  label="Middle_Buttons_Retainer"
  Group = -> [Fusion064]
FEATURE [Part::Cylinder] Cylinder085  label="Cylinder166"
  Angle = 360
  AttacherType = Attacher::AttachEngine3D
  Height = 3.5
  Placement = pos=(46,-9,6) rot=(0,0,1;0rad)
  Radius = 1
FEATURE [Part::Cylinder] Cylinder086  label="Cylinder167"
  Angle = 360
  AttacherType = Attacher::AttachEngine3D
  Height = 2.5
  Placement = pos=(46,-9,8) rot=(0,0,1;0rad)
  Radius = 7
FEATURE [Part::Cylinder] Cylinder087  label="Cylinder168"
  Angle = 360
  AttacherType = Attacher::AttachEngine3D
  Height = 3.5
  Placement = pos=(46,-9,6) rot=(0,0,1;0rad)
  Radius = 2
FEATURE [Part::Cut] Cut110
  Base = -> Cylinder087
  Tool = -> Cylinder085
FEATURE [Part::Fillet] Fillet053
  Base = -> Cylinder086
  Edges = 1 edges r=1.5: [Edge1]
FEATURE [Part::MultiFuse] Fusion065  label="Analog_Button_1"
  Shapes = -> [Fillet053,Cut110]
FEATURE [Part::Cut] Cut111
  Base = -> Cylinder087
  Tool = -> Cylinder085
FEATURE [Part::Fillet] Fillet054
  Base = -> Cylinder086
  Edges = 1 edges r=1.5: [Edge1]
FEATURE [Part::MultiFuse] Fusion066  label="Analog_Button_2"
  Placement = pos=(26,0,0) rot=(0,0,1;0rad)
  Shapes = -> [Fillet054,Cut111]
FEATURE [Part::Box] Box208  label="Left_Top_PCB"
  AttacherType = Attacher::AttachEngine3D
  Height = 25.4
  Length = 12.7
  Placement = pos=(9.5,51,-33) rot=(0,0,1;0rad)
  Width = 1.7
FEATURE [Part::Box] Box209  label="Cube198"
  AttacherType = Attacher::AttachEngine3D
  Height = 3
  Length = 6
  Placement = pos=(2.5,50,-16.5) rot=(0,0,1;0rad)
  Width = 7
FEATURE [Part::Box] Box210  label="Cube199"
  AttacherType = Attacher::AttachEngine3D
  Height = 28
  Length = 2
  Placement = pos=(8.5,50,-34.5) rot=(0,0,1;0rad)
  Width = 1
FEATURE [Part::Box] Box211  label="Cube200"
  AttacherType = Attacher::AttachEngine3D
  Height = 2
  Length = 12
  Placement = pos=(10.5,50,-34.5) rot=(0,0,1;0rad)
  Width = 1
FEATURE [Part::Box] Box212  label="Cube201"
  AttacherType = Attacher::AttachEngine3D
  Height = 2
  Length = 12
  Placement = pos=(10.5,50,-8.5) rot=(0,0,1;0rad)
  Width = 1
FEATURE [Part::Box] Box213  label="Cube202"
  AttacherType = Attacher::AttachEngine3D
  Height = 28
  Length = 1
  Placement = pos=(8.5,51,-34.5) rot=(0,0,1;0rad)
  Width = 2
FEATURE [Part::Box] Box214  label="Cube203"
  AttacherType = Attacher::AttachEngine3D
  Height = 28
  Length = 2
  Placement = pos=(8.5,53,-34.5) rot=(0,0,1;0rad)
  Width = 2
FEATURE [Part::Box] Box215  label="Cube204"
  AttacherType = Attacher::AttachEngine3D
  Height = 1
  Length = 13
  Placement = pos=(9.5,51,-7.5) rot=(0,0,1;0rad)
  Width = 2
FEATURE [Part::Box] Box217  label="Cube206"
  AttacherType = Attacher::AttachEngine3D
  Height = 1
  Length = 13
  Placement = pos=(9.5,51,-34.5) rot=(0,0,1;0rad)
  Width = 2
FEATURE [Part::Box] Box218  label="Cube207"
  AttacherType = Attacher::AttachEngine3D
  Height = 2
  Length = 12
  Placement = pos=(10.5,53,-8.5) rot=(0,0,1;0rad)
  Width = 2
FEATURE [Part::Box] Box219  label="Cube208"
  AttacherType = Attacher::AttachEngine3D
  Height = 2
  Length = 12
  Placement = pos=(10.5,53,-34.5) rot=(0,0,1;0rad)
  Width = 2
FEATURE [Part::Box] Box220  label="Right_Top_PCB"
  AttacherType = Attacher::AttachEngine3D
  Height = 25.4
  Length = 12.7
  Placement = pos=(96.5,51,-33) rot=(0,0,1;0rad)
  Width = 1.7
FEATURE [App::DocumentObjectGroup] Group009  label="Circuit_Boards"
  Group = -> [Fusion004,Fusion008,Box054,Box055,Box056,Box022,Box208,Box220]
FEATURE [Part::Box] Box221  label="Cube209"
  AttacherType = Attacher::AttachEngine3D
  Height = 14
  Length = 6
  Placement = pos=(2.5,57,-27.5) rot=(0,0,1;0rad)
  Width = 2.3
FEATURE [Part::Box] Box222  label="Cube210"
  AttacherType = Attacher::AttachEngine3D
  Height = 3
  Length = 6
  Placement = pos=(2.5,50,-27.5) rot=(0,0,1;0rad)
  Width = 7
FEATURE [Part::Box] Box223  label="Cube211"
  AttacherType = Attacher::AttachEngine3D
  Height = 28
  Length = 6
  Placement = pos=(22.5,57,-34.5) rot=(0,0,1;0rad)
  Width = 2.3
FEATURE [Part::Box] Box224  label="Cube212"
  AttacherType = Attacher::AttachEngine3D
  Height = 28
  Length = 6
  Placement = pos=(22.5,50,-34.5) rot=(0,0,1;0rad)
  Width = 3
FEATURE [Part::Box] Box225  label="Cube213"
  AttacherType = Attacher::AttachEngine3D
  Height = 3
  Length = 6
  Placement = pos=(22.5,53,-34.5) rot=(0,0,1;0rad)
  Width = 4
FEATURE [Part::Box] Box226  label="Cube214"
  AttacherType = Attacher::AttachEngine3D
  Height = 3
  Length = 6
  Placement = pos=(22.5,53,-9.5) rot=(0,0,1;0rad)
  Width = 4
FEATURE [Part::Cylinder] Cylinder088  label="Cylinder169"
  Angle = 360
  AttacherType = Attacher::AttachEngine3D
  Height = 5
  Placement = pos=(5.5,60,-20.5) rot=(1,0,0;1.5708rad)
  Radius = 2
FEATURE [Part::Cylinder] Cylinder089  label="Cylinder170"
  Angle = 360
  AttacherType = Attacher::AttachEngine3D
  Height = 5
  Placement = pos=(25.5,60,-13.5) rot=(1,0,0;1.5708rad)
  Radius = 2
FEATURE [Part::Cylinder] Cylinder090  label="Cylinder171"
  Angle = 360
  AttacherType = Attacher::AttachEngine3D
  Height = 5
  Placement = pos=(25.5,60,-27.5) rot=(1,0,0;1.5708rad)
  Radius = 2
FEATURE [Part::Cylinder] Cylinder091  label="Cylinder172"
  Angle = 360
  AttacherType = Attacher::AttachEngine3D
  Height = 5
  Placement = pos=(25.5,54,-20.5) rot=(1,0,0;1.5708rad)
  Radius = 2
FEATURE [Part::Cut] Cut112
  Base = -> Box221
  Tool = -> Cylinder088
FEATURE [Part::Cut] Cut113
  Base = -> Box223
  Tool = -> Cylinder089
FEATURE [Part::Cut] Cut114
  Base = -> Cut113
  Tool = -> Cylinder090
FEATURE [Part::Cut] Cut115
  Base = -> Box224
  Tool = -> Cylinder091
FEATURE [Part::Fillet] Fillet055
  Base = -> Cut112
  Edges = 2 edges r=2: [Edge10,Edge14]
FEATURE [Part::Fillet] Fillet056
  Base = -> Cut114
  Edges = 2 edges r=2: [Edge12,Edge18]
FEATURE [Part::MultiFuse] Fusion068
  Shapes = -> [Box222,Fillet055,Box209]
FEATURE [Part::MultiFuse] Fusion069  label="Backplane_Top_1"
  Shapes = -> [Box214,Box218,Box219]
FEATURE [Part::MultiFuse] Fusion070
  Shapes = -> [Box211,Box217,Box213,Box210,Box215,Box212]
FEATURE [Part::MultiFuse] Fusion071  label="Backplane_Latch_1"
  Shapes = -> [Cut115,Box226,Fillet056,Box225]
FEATURE [Part::Cut] Cut116  label="Backplane_Reinforcement_003"
  Base = -> Box072
  Tool = -> Cylinder041
FEATURE [Part::Fillet] Fillet057
  Base = -> Box073
  Edges = 2 edges r=6: [Edge4,Edge8]
FEATURE [Part::Cylinder] Cylinder092  label="Cylinder173"
  Angle = 360
  AttacherType = Attacher::AttachEngine3D
  Height = 5
  Placement = pos=(25.5,50,-20.5) rot=(1,0,0;1.5708rad)
  Radius = 2
FEATURE [Part::Cylinder] Cylinder093  label="Cylinder174"
  Angle = 360
  AttacherType = Attacher::AttachEngine3D
  Height = 5
  Placement = pos=(25.5,47,-20.5) rot=(1,0,0;1.5708rad)
  Radius = 4
FEATURE [Part::Cut] Cut117
  Base = -> Fillet057
  Tool = -> Cylinder093
FEATURE [Part::Cut] Cut118
  Base = -> Cut117
  Tool = -> Cylinder092
FEATURE [Part::MultiFuse] Fusion072  label="Main_Backplane_1"
  Shapes = -> [Fusion068,Fusion070,Cut118]
FEATURE [Part::Box] Box227  label="Cube215"
  AttacherType = Attacher::AttachEngine3D
  Height = 4
  Length = 10
  Placement = pos=(28,40,-16) rot=(0,0,1;0rad)
  Width = 10
FEATURE [Part::Cut] Cut119  label="Backplane_Main_001"
  Base = -> Fusion072
  Tool = -> Box227
FEATURE [Part::Box] Box228  label="Cube216"
  AttacherType = Attacher::AttachEngine3D
  Height = 4
  Length = 10
  Placement = pos=(28,40,-16) rot=(0,0,1;0rad)
  Width = 10
FEATURE [Part::Cut] Cut120  label="Backplane_Reinforcement_3"
  Base = -> Cut116
  Tool = -> Box228
FEATURE [Part::Box] Box229  label="Cube217"
  AttacherType = Attacher::AttachEngine3D
  Height = 4
  Length = 10
  Placement = pos=(81,40,-16) rot=(0,0,1;0rad)
  Width = 10
FEATURE [Part::Cut] Cut121
  Base = -> Box094
  Tool = -> Cylinder046
FEATURE [Part::Fillet] Fillet058
  Base = -> Cut121
  Edges = 1 edges r=1.5: [Edge6]
FEATURE [Part::Fillet] Fillet059  label="Backplane_Main_1"
  Base = -> Cut119
  Edges = 1 edges r=1.5: [Edge87]
FEATURE [Part::MultiFuse] Fusion073  label="Backplane_Reinforcement_2"
  Shapes = -> [Fillet058,Fillet012]
FEATURE [Part::Box] Box230  label="Cube218"
  AttacherType = Attacher::AttachEngine3D
  Height = 30
  Length = 30
  Placement = pos=(88,46,-36) rot=(0,0,1;0rad)
  Width = 4
FEATURE [Part::Box] Box231  label="Cube219"
  AttacherType = Attacher::AttachEngine3D
  Height = 4
  Length = 10
  Placement = pos=(81,40,-16) rot=(0,0,1;0rad)
  Width = 10
FEATURE [Part::Cut] Cut123  label="Backplane_Reinforcement_005"
  Base = -> Box072
  Placement = pos=(87,0,0) rot=(0,0,1;0rad)
  Tool = -> Cylinder041
FEATURE [Part::Cut] Cut124  label="Backplane_Reinforcement_6"
  Base = -> Cut123
  Tool = -> Box231
FEATURE [Part::Cut] Cut125
  Base = -> Box230
  Tool = -> Box229
FEATURE [Part::Box] Box232  label="Cube220"
  AttacherType = Attacher::AttachEngine3D
  Height = 3
  Length = 6
  Placement = pos=(22.5,53,-34.5) rot=(0,0,1;0rad)
  Width = 4
FEATURE [Part::Fillet] Fillet060
  Base = -> Cut114
  Edges = 2 edges r=2: [Edge12,Edge18]
FEATURE [Part::Box] Box233  label="Cube221"
  AttacherType = Attacher::AttachEngine3D
  Height = 3
  Length = 6
  Placement = pos=(22.5,53,-9.5) rot=(0,0,1;0rad)
  Width = 4
FEATURE [Part::Cut] Cut126
  Base = -> Box224
  Tool = -> Cylinder091
FEATURE [Part::MultiFuse] Fusion074  label="Backplane_Latch_2"
  Placement = pos=(68,0,0) rot=(0,0,1;0rad)
  Shapes = -> [Cut126,Box233,Fillet060,Box232]
FEATURE [App::DocumentObjectGroup] Group013  label="Latches"
  Group = -> [Fusion052,Fusion057,Fusion058,Fusion056,Fusion055,Fusion054,Fusion053,Fusion059,Fusion060,Fusion061,Fusion071,Fusion074]
FEATURE [Part::Cylinder] Cylinder094  label="Cylinder175"
  Angle = 360
  AttacherType = Attacher::AttachEngine3D
  Height = 5
  Placement = pos=(93.5,47,-20.5) rot=(1,0,0;1.5708rad)
  Radius = 4
FEATURE [Part::Cylinder] Cylinder095  label="Cylinder176"
  Angle = 360
  AttacherType = Attacher::AttachEngine3D
  Height = 5
  Placement = pos=(93.5,50,-20.5) rot=(1,0,0;1.5708rad)
  Radius = 2
FEATURE [Part::Cut] Cut127
  Base = -> Cut125
  Tool = -> Cylinder095
FEATURE [Part::Cut] Cut128
  Base = -> Cut127
  Tool = -> Cylinder094
FEATURE [Part::Box] Box234  label="Cube222"
  AttacherType = Attacher::AttachEngine3D
  Height = 2
  Length = 12
  Placement = pos=(96.5,50,-34.5) rot=(0,0,1;0rad)
  Width = 1
FEATURE [Part::Box] Box235  label="Cube223"
  AttacherType = Attacher::AttachEngine3D
  Height = 1
  Length = 13
  Placement = pos=(96.5,51,-34.5) rot=(0,0,1;0rad)
  Width = 2
FEATURE [Part::Box] Box236  label="Cube224"
  AttacherType = Attacher::AttachEngine3D
  Height = 28
  Length = 1
  Placement = pos=(109.5,51,-34.5) rot=(0,0,1;0rad)
  Width = 2
FEATURE [Part::Box] Box237  label="Cube225"
  AttacherType = Attacher::AttachEngine3D
  Height = 28
  Length = 2
  Placement = pos=(108.5,50,-34.5) rot=(0,0,1;0rad)
  Width = 1
FEATURE [Part::Box] Box238  label="Cube226"
  AttacherType = Attacher::AttachEngine3D
  Height = 1
  Length = 13
  Placement = pos=(96.5,51,-7.5) rot=(0,0,1;0rad)
  Width = 2
FEATURE [Part::Box] Box239  label="Cube227"
  AttacherType = Attacher::AttachEngine3D
  Height = 2
  Length = 12
  Placement = pos=(96.5,50,-8.5) rot=(0,0,1;0rad)
  Width = 1
FEATURE [Part::MultiFuse] Fusion075
  Shapes = -> [Box234,Box235,Box236,Box237,Box238,Box239]
FEATURE [Part::Box] Box240  label="Cube228"
  AttacherType = Attacher::AttachEngine3D
  Height = 3
  Length = 6
  Placement = pos=(110.5,50,-27.5) rot=(0,0,1;0rad)
  Width = 7
FEATURE [Part::Box] Box241  label="Cube229"
  AttacherType = Attacher::AttachEngine3D
  Height = 14
  Length = 6
  Placement = pos=(110.5,57,-27.5) rot=(0,0,1;0rad)
  Width = 2.3
FEATURE [Part::Cylinder] Cylinder096  label="Cylinder177"
  Angle = 360
  AttacherType = Attacher::AttachEngine3D
  Height = 5
  Placement = pos=(113.5,60,-20.5) rot=(1,0,0;1.5708rad)
  Radius = 2
FEATURE [Part::Box] Box242  label="Cube230"
  AttacherType = Attacher::AttachEngine3D
  Height = 3
  Length = 6
  Placement = pos=(110.5,50,-16.5) rot=(0,0,1;0rad)
  Width = 7
FEATURE [Part::Cut] Cut129
  Base = -> Box241
  Tool = -> Cylinder096
FEATURE [Part::Fillet] Fillet061
  Base = -> Cut129
  Edges = 2 edges r=2: [Edge10,Edge14]
FEATURE [Part::Fillet] Fillet062
  Base = -> Cut128
  Edges = 2 edges r=6: [Edge4,Edge23]
FEATURE [Part::MultiFuse] Fusion076  label="Backplane_Main_002"
  Shapes = -> [Box240,Box242,Fillet062,Fillet061,Fusion075]
FEATURE [Part::Fillet] Fillet063  label="Backplane_Main_2"
  Base = -> Fusion076
  Edges = 1 edges r=1.5: [Edge47]
FEATURE [Part::Box] Box243  label="Cube231"
  AttacherType = Attacher::AttachEngine3D
  Height = 28
  Length = 2
  Placement = pos=(108.5,53,-34.5) rot=(0,0,1;0rad)
  Width = 2
FEATURE [Part::Box] Box244  label="Cube232"
  AttacherType = Attacher::AttachEngine3D
  Height = 2
  Length = 12
  Placement = pos=(96.5,53,-8.5) rot=(0,0,1;0rad)
  Width = 2
FEATURE [Part::Box] Box245  label="Cube233"
  AttacherType = Attacher::AttachEngine3D
  Height = 2
  Length = 12
  Placement = pos=(96.5,53,-34.5) rot=(0,0,1;0rad)
  Width = 2
FEATURE [Part::MultiFuse] Fusion077  label="Backplane_Top_2"
  Shapes = -> [Box243,Box244,Box245]
FEATURE [Part::Box] Box249  label="Cube237"
  AttacherType = Attacher::AttachEngine3D
  Height = 9
  Length = 2
  Placement = pos=(118,40,-15) rot=(0,0,1;0rad)
  Width = 10
FEATURE [Part::Cylinder] Cylinder098  label="Cylinder178"
  Angle = 360
  AttacherType = Attacher::AttachEngine3D
  Height = 4
  Placement = pos=(117,31,-15) rot=(0,1,0;1.5708rad)
  Radius = 15
FEATURE [Part::Box] Box250  label="Cube238"
  AttacherType = Attacher::AttachEngine3D
  Height = 13
  Length = 2
  Placement = pos=(118,46,-28) rot=(0,0,1;0rad)
  Width = 4
FEATURE [Part::Box] Box251  label="Cube239"
  AttacherType = Attacher::AttachEngine3D
  Height = 3
  Length = 2
  Placement = pos=(118,36,-6) rot=(0,0,1;0rad)
  Width = 14
FEATURE [Part::Cut] Cut130
  Base = -> Box249
  Tool = -> Cylinder098
FEATURE [Part::MultiFuse] Fusion078
  Shapes = -> [Box251,Cut130,Box250]
FEATURE [Part::Fillet] Fillet064  label="Backplane_Reinforcement_4"
  Base = -> Fusion078
  Edges = 2 edges r=1.5: [Edge2,Edge27]
FEATURE [Part::Box] Box252  label="Cube240"
  AttacherType = Attacher::AttachEngine3D
  Height = 3
  Length = 2
  Placement = pos=(86,36,-6) rot=(0,0,1;0rad)
  Width = 14
FEATURE [Part::Box] Box253  label="Cube241"
  AttacherType = Attacher::AttachEngine3D
  Height = 6
  Length = 2
  Placement = pos=(86,40,-12) rot=(0,0,1;0rad)
  Width = 10
FEATURE [Part::Cylinder] Cylinder099  label="Cylinder179"
  Angle = 360
  AttacherType = Attacher::AttachEngine3D
  Height = 4
  Placement = pos=(85,31,-15) rot=(0,1,0;1.5708rad)
  Radius = 15
FEATURE [Part::Cut] Cut131
  Base = -> Box253
  Tool = -> Cylinder099
FEATURE [Part::MultiFuse] Fusion079
  Shapes = -> [Box252,Cut131]
FEATURE [Part::Fillet] Fillet065  label="Backplane_Reinforcement_5"
  Base = -> Fusion079
  Edges = 2 edges r=1.5: [Edge4,Edge21]
FEATURE [App::DocumentObjectGroup] Group003  label="Top_Buttons_Backplane"
  Group = -> [Fillet011,Fusion069,Cut120,Fillet059,Fusion073,Cut124,Fillet063,Fusion077,Fillet065,Fillet064]
FEATURE [Part::Cylinder] Cylinder101  label="Cylinder180"
  Angle = 360
  AttacherType = Attacher::AttachEngine3D
  Height = 2
  Placement = pos=(93.5,61.3,-27.5) rot=(1,0,0;1.5708rad)
  Radius = 4
FEATURE [Part::Cylinder] Cylinder102  label="Cylinder181"
  Angle = 360
  AttacherType = Attacher::AttachEngine3D
  Height = 2
  Placement = pos=(113.5,61.3,-20.5) rot=(1,0,0;1.5708rad)
  Radius = 4
FEATURE [Part::Cylinder] Cylinder103  label="Cylinder182"
  Angle = 360
  AttacherType = Attacher::AttachEngine3D
  Height = 2
  Placement = pos=(93.5,61.3,-13.5) rot=(1,0,0;1.5708rad)
  Radius = 4
FEATURE [Part::Cylinder] Cylinder104  label="Cylinder183"
  Angle = 360
  AttacherType = Attacher::AttachEngine3D
  Height = 2
  Placement = pos=(113.5,61.3,-20.5) rot=(1,0,0;1.5708rad)
  Radius = 2
FEATURE [Part::Cut] Cut132
  Base = -> Cylinder102
  Placement = pos=(-108,0,0) rot=(0,0,1;0rad)
  Tool = -> Cylinder104
FEATURE [Part::Cylinder] Cylinder105  label="Cylinder184"
  Angle = 360
  AttacherType = Attacher::AttachEngine3D
  Height = 2
  Placement = pos=(93.5,61.3,-13.5) rot=(1,0,0;1.5708rad)
  Radius = 2
FEATURE [Part::Cut] Cut133
  Base = -> Cylinder103
  Placement = pos=(-68,0,0) rot=(0,0,1;0rad)
  Tool = -> Cylinder105
FEATURE [Part::Cylinder] Cylinder106  label="Cylinder185"
  Angle = 360
  AttacherType = Attacher::AttachEngine3D
  Height = 2
  Placement = pos=(93.5,61.3,-27.5) rot=(1,0,0;1.5708rad)
  Radius = 2
FEATURE [Part::Cut] Cut134
  Base = -> Cylinder101
  Placement = pos=(-68,0,0) rot=(0,0,1;0rad)
  Tool = -> Cylinder106
FEATURE [Part::Box] Box255  label="Cube243"
  AttacherType = Attacher::AttachEngine3D
  Height = 8
  Length = 13
  Placement = pos=(9,59.3,-20) rot=(0,0,1;0rad)
  Width = 2
FEATURE [Part::Box] Box256  label="Cube244"
  AttacherType = Attacher::AttachEngine3D
  Height = 8
  Length = 13
  Placement = pos=(97,59.3,-31) rot=(0,0,1;0rad)
  Width = 2
FEATURE [Part::Box] Box257  label="Cube245"
  AttacherType = Attacher::AttachEngine3D
  Height = 25
  Length = 15
  Placement = pos=(8,59.3,-33) rot=(0,0,1;0rad)
  Width = 2
FEATURE [Part::Cut] Cut136
  Tool = -> Box256
FEATURE [Part::Box] Box259  label="Cube247"
  AttacherType = Attacher::AttachEngine3D
  Height = 10
  Length = 13
  Placement = pos=(97,57.3,-21) rot=(0,0,1;0rad)
  Width = 1.5
FEATURE [Part::Fillet] Fillet068  label="Top_Right_Button_Retainer"
  Base = -> Cut136
  Edges = 4 edges r=2: [Edge35,Edge46,Edge87,Edge95]
FEATURE [Part::MultiFuse] Fusion083
  Shapes = -> [Cut134,Box257,Cut132,Cut133]
FEATURE [Part::Box] Box262  label="Cube250"
  AttacherType = Attacher::AttachEngine3D
  Height = 8
  Length = 13
  Placement = pos=(9,59.3,-31) rot=(0,0,1;0rad)
  Width = 2
FEATURE [Part::Cut] Cut137
  Base = -> Fusion083
  Tool = -> Box255
FEATURE [Part::Cut] Cut138
  Base = -> Cut137
  Tool = -> Box262
FEATURE [Part::Fillet] Fillet069  label="Top_Left_Button_Retainer"
  Base = -> Cut138
  Edges = 4 edges r=2: [Edge20,Edge51,Edge99,Edge100]
FEATURE [Part::Box] Box263  label="Cube251"
  AttacherType = Attacher::AttachEngine3D
  Height = 7
  Length = 12
  Placement = pos=(97.5,57.3,-19.5) rot=(0,0,1;0rad)
  Width = 5
FEATURE [Part::MultiFuse] Fusion084
  Shapes = -> [Box259,Box263]
FEATURE [Part::Fillet] Fillet070  label="Top_Button_1"
  Base = -> Fusion084
  Edges = 4 edges r=1: [Edge22,Edge24,Edge27,Edge28]
FEATURE [Part::MultiFuse] Fusion085
  Shapes = -> [Box259,Box263]
FEATURE [Part::Fillet] Fillet071  label="Top_Button_2"
  Base = -> Fusion085
  Edges = 4 edges r=1: [Edge22,Edge24,Edge27,Edge28]
  Placement = pos=(0,0,-11) rot=(0,0,1;0rad)
FEATURE [Part::MultiFuse] Fusion086
  Shapes = -> [Box259,Box263]
FEATURE [Part::Fillet] Fillet072  label="Top_Button_3"
  Base = -> Fusion086
  Edges = 4 edges r=1: [Edge22,Edge24,Edge27,Edge28]
  Placement = pos=(-88,0,0) rot=(0,0,1;0rad)
FEATURE [Part::MultiFuse] Fusion087
  Shapes = -> [Box259,Box263]
FEATURE [Part::Fillet] Fillet073  label="Top_Button_4"
  Base = -> Fusion087
  Edges = 4 edges r=1: [Edge22,Edge24,Edge27,Edge28]
  Placement = pos=(-88,0,-11) rot=(0,0,1;0rad)
FEATURE [App::DocumentObjectGroup] Group  label="Buttons"
  Group = -> [Cut071,Cut072,Cut073,Cut074,Fusion062,Fusion063,Fusion065,Fusion066,Fillet070,Fillet071,Fillet072,Fillet073]
FEATURE [App::DocumentObjectGroup] Group015  label="Top_Button_Retainers"
  Group = -> [Fillet069,Fillet068]
